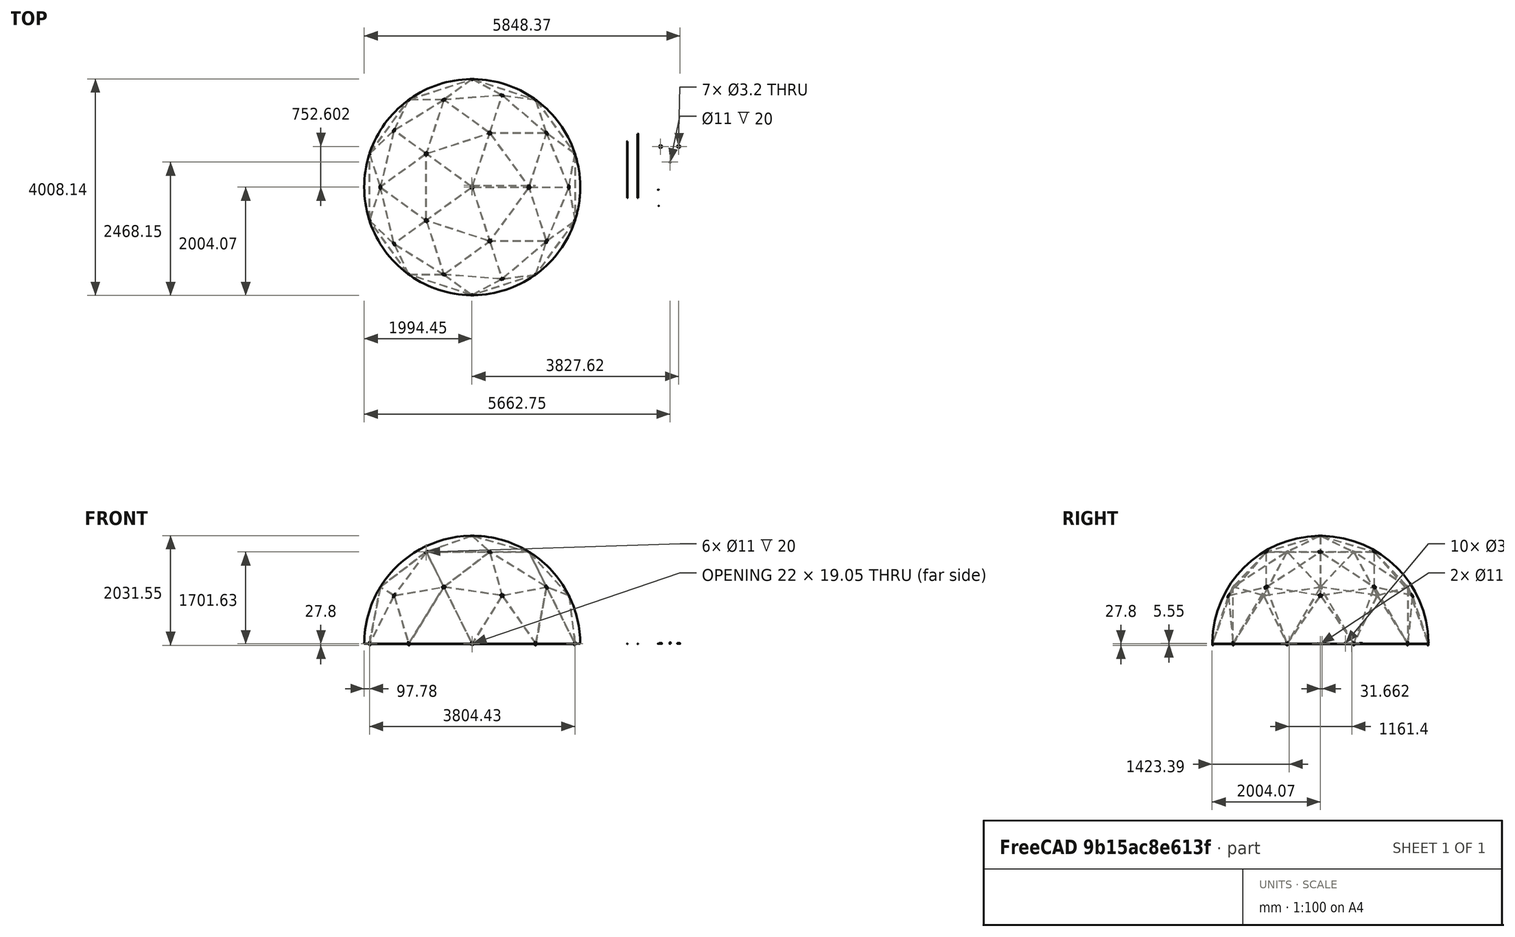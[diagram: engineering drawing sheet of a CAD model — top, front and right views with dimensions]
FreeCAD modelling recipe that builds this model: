
FCSTD DOCUMENT  (FreeCAD 0.19R)
Label: Ejemplo1top
License: All rights reserved
LicenseURL: http://en.wikipedia.org/wiki/All_rights_reserved
objects: Part::Feature×235, Part::Part2DObjectPython×138, App::DocumentObjectGroup×21, App::Annotation×18, Part::Mirroring×7, App::FeaturePython×4, Part::Sphere×1, Part::Cylinder×1
note: 382 computed .brp shape members not serialized (recipe doc carries the construction recipe); baked Part::Feature solids carry a one-line shape summary decoded from their .brp

FEATURE [Part::Part2DObjectPython] Line  # Draft 2D object (typed FeaturePython)
  ChamferSize = 0
  Closed = false
  End = (-1902.16,617.998,0)
  FilletRadius = 0
  Length = 1236.1
  MakeFace = true
  MapMode = 5
  Placement = pos=(-1154.86,1595.54,0) rot=(0,0,-1;0.628319rad)
  Points = (2) [(-30,6,0),(-30,-1230.1,0)]
  Start = (-1175.6,1618.02,0)
  Subdivisions = 0
FEATURE [Part::Part2DObjectPython] Line003  # Draft 2D object (typed FeaturePython)
  ChamferSize = 0
  Closed = false
  End = (-1175.6,1618.02,0)
  FilletRadius = 0
  Length = 1236.1
  MakeFace = true
  MapMode = 5
  Placement = pos=(3.56417,1969.61,0) rot=(0,0,-1;1.25664rad)
  Points = (2) [(-30,6,0),(-30,-1230.1,0)]
  Start = (3.56741e-11,2000,0)
  Subdivisions = 0
FEATURE [Part::Mirroring] Part__Mirroring  label="Line (Mirror #1)"
  Base = (0,0,0)
  Normal = (1,0,0)
  Source = -> Line
FEATURE [Part::Mirroring] Part__Mirroring001  label="Line003 (Mirror #2)"
  Base = (0,0,0)
  Normal = (1,0,0)
  Source = -> Line003
FEATURE [Part::Mirroring] Part__Mirroring002  label="Line (Mirror #3)"
  Base = (0,0,0)
  Normal = (0,1,0)
  Source = -> Line
FEATURE [Part::Mirroring] Part__Mirroring003  label="Line003 (Mirror #4)"
  Base = (0,0,0)
  Normal = (0,1,0)
  Source = -> Line003
FEATURE [Part::Mirroring] Part__Mirroring004  label="Line (Mirror #5)"
  Base = (0,0,0)
  Normal = (0,1,0)
  Source = -> Part__Mirroring
FEATURE [Part::Mirroring] Part__Mirroring005  label="Line003 (Mirror #6)"
  Base = (0,0,0)
  Normal = (0,1,0)
  Source = -> Part__Mirroring001
FEATURE [Part::Part2DObjectPython] Line006  # Draft 2D object (typed FeaturePython)
  ChamferSize = 0
  Closed = false
  End = (-1902.16,-617.998,0)
  FilletRadius = 0
  Length = 1236
  MakeFace = true
  MapMode = 5
  Points = (2) [(-1902.16,617.998,0),(-1902.16,-617.998,0)]
  Start = (-1902.16,617.998,0)
  Subdivisions = 0
FEATURE [Part::Sphere] Sphere
  Angle1 = 0
  Angle2 = 90
  Angle3 = 360
  AttacherType = Attacher::AttachEngine3D
  Radius = 2000
FEATURE [Part::Part2DObjectPython] Line014  # Draft 2D object (typed FeaturePython)
  ChamferSize = 0
  Closed = false
  End = (1902.16,3e-10,0)
  FilletRadius = 0
  Length = 1902.16
  MakeFace = true
  MapMode = 5
  Points = (2) [(-1.99975e-10,3.00133e-10,0),(1902.16,3.0025e-10,0)]
  Start = (0,0,0)
  Subdivisions = 0
FEATURE [Part::Part2DObjectPython] Line015  # Draft 2D object (typed FeaturePython)
  ChamferSize = 0
  Closed = false
  End = (1902.16,3e-10,0)
  FilletRadius = 0
  Length = 1902.16
  MakeFace = true
  MapMode = 5
  Points = (2) [(-1.99975e-10,3.00133e-10,0),(1902.16,3.0025e-10,0)]
  Start = (0,0,0)
  Subdivisions = 0
FEATURE [Part::Part2DObjectPython] Line016  # Draft 2D object (typed FeaturePython)
  ChamferSize = 0
  Closed = false
  End = (587.785,1809.02,0)
  FilletRadius = 0
  Length = 1902.11
  MakeFace = true
  MapMode = 5
  Points = (2) [(-1.99975e-10,3.00133e-10,0),(587.785,1809.02,0)]
  Start = (0,0,0)
  Subdivisions = 0
FEATURE [Part::Part2DObjectPython] Line017  # Draft 2D object (typed FeaturePython)
  ChamferSize = 0
  Closed = false
  End = (-1538.86,1118.05,0)
  FilletRadius = 0
  Length = 1902.13
  MakeFace = true
  MapMode = 5
  Points = (2) [(-1.99975e-10,3.00133e-10,0),(-1538.86,1118.05,0)]
  Start = (0,0,0)
  Subdivisions = 0
FEATURE [Part::Part2DObjectPython] Line018  # Draft 2D object (typed FeaturePython)
  ChamferSize = 0
  Closed = false
  End = (-1538.86,-1118.05,0)
  FilletRadius = 0
  Length = 1902.13
  MakeFace = true
  MapMode = 5
  Points = (2) [(-1.99975e-10,3.00133e-10,0),(-1538.86,-1118.05,0)]
  Start = (0,0,0)
  Subdivisions = 0
FEATURE [Part::Part2DObjectPython] Line019  # Draft 2D object (typed FeaturePython)
  ChamferSize = 0
  Closed = false
  End = (-577.454,-703.099,0)
  FilletRadius = 0
  Length = 1093.1
  MakeFace = true
  MapMode = 5
  Placement = pos=(1075.61,-2380.95,0) rot=(0,0,-1;0.581932rad)
  Points = (2) [(-2300,-600,0),(-2303.19,493.095,0)]
  Start = (-1175.6,-1618.02,0)
  Subdivisions = 0
FEATURE [Part::Part2DObjectPython] Line022  # Draft 2D object (typed FeaturePython)
  ChamferSize = 0
  Closed = false
  End = (587.8,-1809.01,0)
  FilletRadius = 0
  Length = 1902.11
  MakeFace = true
  MapMode = 5
  Points = (2) [(-1.99975e-10,3.00133e-10,0),(587.8,-1809.01,0)]
  Start = (0,0,0)
  Subdivisions = 0
FEATURE [Part::Part2DObjectPython] Line023  # Draft 2D object (typed FeaturePython)
  ChamferSize = 0
  Closed = false
  End = (0,0,2000)
  FilletRadius = 0
  Length = 2000
  MakeFace = true
  MapMode = 5
  Points = (2) [(-1.99975e-10,3.00133e-10,0),(1.22465e-13,-2.99952e-29,2000)]
  Start = (0,0,0)
  Subdivisions = 0
FEATURE [Part::Part2DObjectPython] DWire001  # Draft 2D object (typed FeaturePython)
  ChamferSize = 0
  Closed = true
  End = (1902.16,617.998,0)
  FilletRadius = 0
  Length = 3422.2
  MakeFace = true
  MapMode = 5
  Points = (3) [(1902.16,-617.998,0),(1788.83,-9.64734e-10,894.484),(1902.16,617.998,0)]
  Start = (1902.16,-617.998,0)
  Subdivisions = 0
FEATURE [Part::Part2DObjectPython] DWire  # Draft 2D object (typed FeaturePython)
  ChamferSize = 0
  Closed = true
  End = (587.785,1809.02,0)
  FilletRadius = 0
  Length = 6662.19
  MakeFace = true
  MapMode = 5
  Points = (3) [(1.22465e-13,0,2000),(-1.99975e-10,3.00133e-10,0),(587.785,1809.02,0)]
  Start = (0,0,2000)
  Subdivisions = 0
FEATURE [Part::Mirroring] Part__Mirroring006  label="DWire003 (Mirror #7)"
  Base = (0,0,0)
  Normal = (0,1,0)
FEATURE [Part::Part2DObjectPython] Arc  # Draft 2D object (typed FeaturePython)
  FirstAngle = 56.8247
  LastAngle = 105.817
  MakeFace = true
  MapMode = 5
  Placement = pos=(-1175.6,-1618.02,0) rot=(0,0,1;0rad)
  Radius = 1093.1
FEATURE [Part::Part2DObjectPython] Line026  # Draft 2D object (typed FeaturePython)
  ChamferSize = 0
  Closed = false
  End = (-1902.16,-617.998,0)
  FilletRadius = 0
  Length = 1093.15
  MakeFace = true
  MapMode = 5
  Points = (2) [(-809.424,-588.081,0),(-1902.16,-617.998,0)]
  Start = (-809.424,-588.081,0)
  Subdivisions = 0
FEATURE [Part::Part2DObjectPython] DWire004  # Draft 2D object (typed FeaturePython)
  ChamferSize = 0
  Closed = true
  End = (-1538.86,-1118.05,0)
  FilletRadius = 0
  Length = 6662.22
  MakeFace = true
  MapMode = 5
  Points = (3) [(1.22465e-13,0,2000),(-1.99975e-10,3.00133e-10,0),(-1538.86,-1118.05,0)]
  Start = (0,0,2000)
  Subdivisions = 0
FEATURE [Part::Part2DObjectPython] DWire005  # Draft 2D object (typed FeaturePython)
  ChamferSize = 0
  Closed = true
  End = (-1175.6,-1618.02,0)
  FilletRadius = 0
  Length = 3422.35
  MakeFace = true
  MapMode = 5
  Points = (3) [(-1902.16,-617.998,0),(-1447.19,-1051.45,894.481),(-1175.6,-1618.02,0)]
  Start = (-1902.16,-617.998,0)
  Subdivisions = 0
FEATURE [Part::Part2DObjectPython] Line027  # Draft 2D object (typed FeaturePython)
  ChamferSize = 0
  Closed = false
  End = (-878.683,234.127,0)
  FilletRadius = 0
  Length = 1093.1
  MakeFace = true
  MapMode = 5
  Placement = pos=(-2154.97,-1745.49,0) rot=(0,0,-1;1.93254rad)
  Points = (2) [(-2300,-600,0),(-2303.19,493.095,0)]
  Start = (-1902.16,617.998,0)
  Subdivisions = 0
FEATURE [Part::Part2DObjectPython] Arc003  # Draft 2D object (typed FeaturePython)
  FirstAngle = -20.5593
  LastAngle = 28.7005
  MakeFace = true
  MapMode = 5
  Placement = pos=(-1902.16,617.998,0) rot=(0,0,1;0rad)
  Radius = 1093.1
FEATURE [Part::Part2DObjectPython] DWire006  # Draft 2D object (typed FeaturePython)
  ChamferSize = 0
  Closed = true
  End = (-1538.86,1118.05,0)
  FilletRadius = 0
  Length = 6662.22
  MakeFace = true
  MapMode = 5
  Points = (3) [(1.22465e-13,0,2000),(-1.99975e-10,3.00133e-10,0),(-1538.86,1118.05,0)]
  Start = (0,0,2000)
  Subdivisions = 0
FEATURE [Part::Part2DObjectPython] DWire007  # Draft 2D object (typed FeaturePython)
  ChamferSize = 0
  Closed = true
  End = (-1902.16,617.998,0)
  FilletRadius = 0
  Length = 3422.25
  MakeFace = true
  MapMode = 5
  Points = (3) [(-1175.6,1618.02,0),(-1447.21,1051.46,894.426),(-1902.16,617.998,0)]
  Start = (-1175.6,1618.02,0)
  Subdivisions = 0
FEATURE [Part::Part2DObjectPython] DWire008  # Draft 2D object (typed FeaturePython)
  ChamferSize = 0
  Closed = true
  End = (324.937,-1000.03,1701.28)
  FilletRadius = 0
  Length = 3422.31
  MakeFace = true
  MapMode = 5
  Points = (3) [(2.23523e-10,2.82703e-10,2000),(-850.675,-618.052,1701.28),(324.937,-1000.03,1701.28)]
  Start = (2.24e-10,2.83e-10,2000)
  Subdivisions = 0
FEATURE [Part::Part2DObjectPython] DWire009  # Draft 2D object (typed FeaturePython)
  ChamferSize = 0
  Closed = true
  End = (-2e-10,3e-10,2000)
  FilletRadius = 0
  Length = 3422.3
  MakeFace = true
  MapMode = 5
  Points = (3) [(324.937,-1000.03,1701.28),(1051.49,1.3321e-09,1701.28),(-1.99876e-10,3.00061e-10,2000)]
  Start = (324.937,-1000.03,1701.28)
  Subdivisions = 0
FEATURE [Part::Part2DObjectPython] DWire010  # Draft 2D object (typed FeaturePython)
  ChamferSize = 0
  Closed = true
  End = (324.929,1000.03,1701.28)
  FilletRadius = 0
  Length = 3422.3
  MakeFace = true
  MapMode = 5
  Points = (3) [(-1.99876e-10,3.00061e-10,2000),(1051.49,1.3321e-09,1701.28),(324.929,1000.03,1701.28)]
  Start = (-2e-10,3e-10,2000)
  Subdivisions = 0
FEATURE [Part::Part2DObjectPython] DWire011  # Draft 2D object (typed FeaturePython)
  ChamferSize = 0
  Closed = true
  End = (-850.675,618.052,1701.28)
  FilletRadius = 0
  Length = 3422.3
  MakeFace = true
  MapMode = 5
  Points = (3) [(-1.99876e-10,3.00061e-10,2000),(324.929,1000.03,1701.28),(-850.675,618.052,1701.28)]
  Start = (-2e-10,3e-10,2000)
  Subdivisions = 0
FEATURE [Part::Part2DObjectPython] DWire012  # Draft 2D object (typed FeaturePython)
  ChamferSize = 0
  Closed = true
  End = (-850.675,-618.052,1701.28)
  FilletRadius = 0
  Length = 3422.3
  MakeFace = true
  MapMode = 5
  Points = (3) [(-1.99876e-10,3.00061e-10,2000),(-850.675,618.052,1701.28),(-850.675,-618.052,1701.28)]
  Start = (-2e-10,3e-10,2000)
  Subdivisions = 0
FEATURE [Part::Part2DObjectPython] Line040  # Draft 2D object (typed FeaturePython)
  ChamferSize = 0
  Closed = false
  End = (-1447.19,-1051.45,894.481)
  FilletRadius = 0
  Length = 1092.97
  MakeFace = true
  MapMode = 5
  Points = (2) [(-850.675,-618.052,1701.28),(-1447.19,-1051.45,894.481)]
  Start = (-850.675,-618.052,1701.28)
  Subdivisions = 0
FEATURE [Part::Part2DObjectPython] DWire013  # Draft 2D object (typed FeaturePython)
  ChamferSize = 0
  Closed = true
  End = (0,0,2000)
  FilletRadius = 0
  Length = 6662.22
  MakeFace = true
  MapMode = 5
  Points = (3) [(1538.88,-1118.01,0),(-1.99975e-10,3.00133e-10,0),(1.22465e-13,0,2000)]
  Start = (1538.88,-1118.01,0)
  Subdivisions = 0
FEATURE [Part::Part2DObjectPython] Arc007  # Draft 2D object (typed FeaturePython)
  FirstAngle = -90
  LastAngle = 6.05971
  MakeFace = true
  MapMode = 5
  Placement = pos=(7.36405e-11,1.01362e-10,0) rot=(0.223911,0.689153,0.689153;2.70104rad)
  Radius = 2000
  Support = -> [DWire013]
FEATURE [Part::Part2DObjectPython] DWire014  # Draft 2D object (typed FeaturePython)
  ChamferSize = 0
  Closed = true
  End = (1902.16,-617.998,0)
  FilletRadius = 0
  Length = 3708.32
  MakeFace = true
  MapMode = 5
  Points = (3) [(1175.6,-1618.02,0),(1376.39,-999.957,1051.5),(1902.16,-617.998,0)]
  Start = (1175.6,-1618.02,0)
  Subdivisions = 0
FEATURE [Part::Part2DObjectPython] DWire015  # Draft 2D object (typed FeaturePython)
  ChamferSize = 0
  Closed = true
  End = (1051.49,1.332e-09,1701.28)
  FilletRadius = 0
  Length = 3708.12
  MakeFace = true
  MapMode = 5
  Points = (3) [(1376.39,-999.957,1051.5),(324.937,-1000.03,1701.28),(1051.49,1.3321e-09,1701.28)]
  Start = (1376.39,-999.957,1051.5)
  Subdivisions = 0
FEATURE [Part::Part2DObjectPython] DWire016  # Draft 2D object (typed FeaturePython)
  ChamferSize = 0
  Closed = true
  End = (1175.6,-1618.02,0)
  FilletRadius = 0
  Length = 3422.29
  MakeFace = true
  MapMode = 5
  Points = (3) [(552.796,-1701.28,894.456),(1376.39,-999.957,1051.5),(1175.6,-1618.02,0)]
  Start = (552.796,-1701.28,894.456)
  Subdivisions = 0
FEATURE [Part::Part2DObjectPython] DWire017  # Draft 2D object (typed FeaturePython)
  ChamferSize = 0
  Closed = true
  End = (1902.16,-617.998,0)
  FilletRadius = 0
  Length = 3422.23
  MakeFace = true
  MapMode = 5
  Points = (3) [(1376.39,-999.957,1051.5),(1788.83,-9.64734e-10,894.484),(1902.16,-617.998,0)]
  Start = (1376.39,-999.957,1051.5)
  Subdivisions = 0
FEATURE [Part::Part2DObjectPython] DWire018  # Draft 2D object (typed FeaturePython)
  ChamferSize = 0
  Closed = true
  End = (1376.39,-999.957,1051.5)
  FilletRadius = 0
  Length = 3422.11
  MakeFace = true
  MapMode = 5
  Points = (3) [(324.937,-1000.03,1701.28),(552.796,-1701.28,894.456),(1376.39,-999.957,1051.5)]
  Start = (324.937,-1000.03,1701.28)
  Subdivisions = 0
FEATURE [Part::Part2DObjectPython] DWire019  # Draft 2D object (typed FeaturePython)
  ChamferSize = 0
  Closed = true
  End = (1788.83,-9.65e-10,894.484)
  FilletRadius = 0
  Length = 3421.98
  MakeFace = true
  MapMode = 5
  Points = (3) [(1376.39,-999.957,1051.5),(1051.49,1.3321e-09,1701.28),(1788.83,-9.64734e-10,894.484)]
  Start = (1376.39,-999.957,1051.5)
  Subdivisions = 0
FEATURE [Part::Part2DObjectPython] DWire020  # Draft 2D object (typed FeaturePython)
  ChamferSize = 0
  Closed = true
  End = (1175.6,1618.02,0)
  FilletRadius = 0
  Length = 3708.32
  MakeFace = true
  MapMode = 5
  Points = (3) [(1902.16,617.998,0),(1376.39,999.957,1051.5),(1175.6,1618.02,0)]
  Start = (1902.16,617.998,0)
  Subdivisions = 0
FEATURE [Part::Part2DObjectPython] DWire021  # Draft 2D object (typed FeaturePython)
  ChamferSize = 0
  Closed = true
  End = (-1175.6,1618.02,0)
  FilletRadius = 0
  Length = 3708.32
  MakeFace = true
  MapMode = 5
  Points = (3) [(-525.738,1618.01,1051.5),(3.56977e-11,2000,0),(-1175.6,1618.02,0)]
  Start = (-525.738,1618.01,1051.5)
  Subdivisions = 0
FEATURE [Part::Part2DObjectPython] DWire022  # Draft 2D object (typed FeaturePython)
  ChamferSize = 0
  Closed = true
  End = (-1902.16,-617.998,0)
  FilletRadius = 0
  Length = 3708.18
  MakeFace = true
  MapMode = 5
  Points = (3) [(-1701.28,-1.02242e-09,1051.5),(-1902.16,617.998,0),(-1902.16,-617.998,0)]
  Start = (-1701.28,-1.022e-09,1051.5)
  Subdivisions = 0
FEATURE [Part::Part2DObjectPython] DWire023  # Draft 2D object (typed FeaturePython)
  ChamferSize = 0
  Closed = true
  End = (-3.6e-11,-2000,0)
  FilletRadius = 0
  Length = 3708.32
  MakeFace = true
  MapMode = 5
  Points = (3) [(-525.738,-1618.01,1051.5),(-1175.6,-1618.02,0),(-3.5925e-11,-2000,0)]
  Start = (-525.738,-1618.01,1051.5)
  Subdivisions = 0
FEATURE [Part::Part2DObjectPython] DWire024  # Draft 2D object (typed FeaturePython)
  ChamferSize = 0
  Closed = true
  End = (324.929,1000.03,1701.28)
  FilletRadius = 0
  Length = 3708.14
  MakeFace = true
  MapMode = 5
  Points = (3) [(1051.49,1.3321e-09,1701.28),(1376.39,999.957,1051.5),(324.929,1000.03,1701.28)]
  Start = (1051.49,1.332e-09,1701.28)
  Subdivisions = 0
FEATURE [Part::Part2DObjectPython] DWire025  # Draft 2D object (typed FeaturePython)
  ChamferSize = 0
  Closed = true
  End = (1376.39,999.957,1051.5)
  FilletRadius = 0
  Length = 3421.98
  MakeFace = true
  MapMode = 5
  Points = (3) [(1051.49,1.3321e-09,1701.28),(1788.83,-9.64734e-10,894.484),(1376.39,999.957,1051.5)]
  Start = (1051.49,1.332e-09,1701.28)
  Subdivisions = 0
FEATURE [Part::Part2DObjectPython] DWire026  # Draft 2D object (typed FeaturePython)
  ChamferSize = 0
  Closed = true
  End = (1376.39,999.957,1051.5)
  FilletRadius = 0
  Length = 3422.23
  MakeFace = true
  MapMode = 5
  Points = (3) [(1788.83,-9.64734e-10,894.484),(1902.16,617.998,0),(1376.39,999.957,1051.5)]
  Start = (1788.83,-9.65e-10,894.484)
  Subdivisions = 0
FEATURE [Part::Part2DObjectPython] DWire027  # Draft 2D object (typed FeaturePython)
  ChamferSize = 0
  Closed = true
  End = (552.796,1701.28,894.456)
  FilletRadius = 0
  Length = 3422.29
  MakeFace = true
  MapMode = 5
  Points = (3) [(1376.39,999.957,1051.5),(1175.6,1618.02,0),(552.796,1701.28,894.456)]
  Start = (1376.39,999.957,1051.5)
  Subdivisions = 0
FEATURE [Part::Part2DObjectPython] DWire028  # Draft 2D object (typed FeaturePython)
  ChamferSize = 0
  Closed = true
  End = (552.796,1701.28,894.456)
  FilletRadius = 0
  Length = 3422.12
  MakeFace = true
  MapMode = 5
  Points = (3) [(324.929,1000.03,1701.28),(1376.39,999.957,1051.5),(552.796,1701.28,894.456)]
  Start = (324.929,1000.03,1701.28)
  Subdivisions = 0
FEATURE [Part::Part2DObjectPython] DWire029  # Draft 2D object (typed FeaturePython)
  ChamferSize = 0
  Closed = true
  End = (-3.6e-11,2000,0)
  FilletRadius = 0
  Length = 3422.29
  MakeFace = true
  MapMode = 5
  Points = (3) [(-525.738,1618.01,1051.5),(552.796,1701.28,894.456),(-3.5925e-11,2000,0)]
  Start = (-525.738,1618.01,1051.5)
  Subdivisions = 0
FEATURE [Part::Part2DObjectPython] DWire030  # Draft 2D object (typed FeaturePython)
  ChamferSize = 0
  Closed = true
  End = (-525.738,1618.01,1051.5)
  FilletRadius = 0
  Length = 3422.11
  MakeFace = true
  MapMode = 5
  Points = (3) [(324.929,1000.03,1701.28),(552.796,1701.28,894.456),(-525.738,1618.01,1051.5)]
  Start = (324.929,1000.03,1701.28)
  Subdivisions = 0
FEATURE [Part::Part2DObjectPython] DWire031  # Draft 2D object (typed FeaturePython)
  ChamferSize = 0
  Closed = true
  End = (-850.675,618.052,1701.28)
  FilletRadius = 0
  Length = 3708.14
  MakeFace = true
  MapMode = 5
  Points = (3) [(324.929,1000.03,1701.28),(-525.738,1618.01,1051.5),(-850.675,618.052,1701.28)]
  Start = (324.929,1000.03,1701.28)
  Subdivisions = 0
FEATURE [Part::Part2DObjectPython] DWire032  # Draft 2D object (typed FeaturePython)
  ChamferSize = 0
  Closed = true
  End = (-1447.21,1051.46,894.426)
  FilletRadius = 0
  Length = 3422.21
  MakeFace = true
  MapMode = 5
  Points = (3) [(-525.738,1618.01,1051.5),(-1175.6,1618.02,0),(-1447.21,1051.46,894.426)]
  Start = (-525.738,1618.01,1051.5)
  Subdivisions = 0
FEATURE [Part::Part2DObjectPython] DWire033  # Draft 2D object (typed FeaturePython)
  ChamferSize = 0
  Closed = true
  End = (-1447.21,1051.46,894.426)
  FilletRadius = 0
  Length = 3422.1
  MakeFace = true
  MapMode = 5
  Points = (3) [(-525.738,1618.01,1051.5),(-850.675,618.052,1701.28),(-1447.21,1051.46,894.426)]
  Start = (-525.738,1618.01,1051.5)
  Subdivisions = 0
FEATURE [Part::Part2DObjectPython] DWire034  # Draft 2D object (typed FeaturePython)
  ChamferSize = 0
  Closed = true
  End = (-1701.28,-1.022e-09,1051.5)
  FilletRadius = 0
  Length = 3422.12
  MakeFace = true
  MapMode = 5
  Points = (3) [(-850.675,618.052,1701.28),(-1447.21,1051.46,894.426),(-1701.28,-1.02242e-09,1051.5)]
  Start = (-850.675,618.052,1701.28)
  Subdivisions = 0
FEATURE [Part::Part2DObjectPython] DWire035  # Draft 2D object (typed FeaturePython)
  ChamferSize = 0
  Closed = true
  End = (-1701.28,-1.022e-09,1051.5)
  FilletRadius = 0
  Length = 3422.26
  MakeFace = true
  MapMode = 5
  Points = (3) [(-1447.21,1051.46,894.426),(-1902.16,617.998,0),(-1701.28,-1.02242e-09,1051.5)]
  Start = (-1447.21,1051.46,894.426)
  Subdivisions = 0
FEATURE [Part::Part2DObjectPython] DWire036  # Draft 2D object (typed FeaturePython)
  ChamferSize = 0
  Closed = true
  End = (-850.675,-618.052,1701.28)
  FilletRadius = 0
  Length = 3708.14
  MakeFace = true
  MapMode = 5
  Points = (3) [(-850.675,618.052,1701.28),(-1701.28,-1.02242e-09,1051.5),(-850.675,-618.052,1701.28)]
  Start = (-850.675,618.052,1701.28)
  Subdivisions = 0
FEATURE [Part::Part2DObjectPython] DWire037  # Draft 2D object (typed FeaturePython)
  ChamferSize = 0
  Closed = true
  End = (-1447.19,-1051.45,894.481)
  FilletRadius = 0
  Length = 3422.04
  MakeFace = true
  MapMode = 5
  Points = (3) [(-1701.28,-1.02242e-09,1051.5),(-850.675,-618.052,1701.28),(-1447.19,-1051.45,894.481)]
  Start = (-1701.28,-1.022e-09,1051.5)
  Subdivisions = 0
FEATURE [Part::Part2DObjectPython] DWire038  # Draft 2D object (typed FeaturePython)
  ChamferSize = 0
  Closed = true
  End = (-1447.19,-1051.45,894.481)
  FilletRadius = 0
  Length = 3422.29
  MakeFace = true
  MapMode = 5
  Points = (3) [(-1701.28,-1.02242e-09,1051.5),(-1902.16,-617.998,0),(-1447.19,-1051.45,894.481)]
  Start = (-1701.28,-1.022e-09,1051.5)
  Subdivisions = 0
FEATURE [Part::Part2DObjectPython] DWire039  # Draft 2D object (typed FeaturePython)
  ChamferSize = 0
  Closed = true
  End = (-525.738,-1618.01,1051.5)
  FilletRadius = 0
  Length = 3422.02
  MakeFace = true
  MapMode = 5
  Points = (3) [(-850.675,-618.052,1701.28),(-1447.19,-1051.45,894.481),(-525.738,-1618.01,1051.5)]
  Start = (-850.675,-618.052,1701.28)
  Subdivisions = 0
FEATURE [Part::Part2DObjectPython] DWire040  # Draft 2D object (typed FeaturePython)
  ChamferSize = 0
  Closed = true
  End = (324.937,-1000.03,1701.28)
  FilletRadius = 0
  Length = 3708.15
  MakeFace = true
  MapMode = 5
  Points = (3) [(-850.675,-618.052,1701.28),(-525.738,-1618.01,1051.5),(324.937,-1000.03,1701.28)]
  Start = (-850.675,-618.052,1701.28)
  Subdivisions = 0
FEATURE [Part::Part2DObjectPython] DWire041  # Draft 2D object (typed FeaturePython)
  ChamferSize = 0
  Closed = true
  End = (-1447.19,-1051.45,894.481)
  FilletRadius = 0
  Length = 3422.24
  MakeFace = true
  MapMode = 5
  Points = (3) [(-525.738,-1618.01,1051.5),(-1175.6,-1618.02,0),(-1447.19,-1051.45,894.481)]
  Start = (-525.738,-1618.01,1051.5)
  Subdivisions = 0
FEATURE [Part::Part2DObjectPython] DWire042  # Draft 2D object (typed FeaturePython)
  ChamferSize = 0
  Closed = true
  End = (552.796,-1701.28,894.456)
  FilletRadius = 0
  Length = 3422.12
  MakeFace = true
  MapMode = 5
  Points = (3) [(-525.738,-1618.01,1051.5),(324.937,-1000.03,1701.28),(552.796,-1701.28,894.456)]
  Start = (-525.738,-1618.01,1051.5)
  Subdivisions = 0
FEATURE [Part::Part2DObjectPython] DWire043  # Draft 2D object (typed FeaturePython)
  ChamferSize = 0
  Closed = true
  End = (552.796,-1701.28,894.456)
  FilletRadius = 0
  Length = 3422.29
  MakeFace = true
  MapMode = 5
  Points = (3) [(-525.738,-1618.01,1051.5),(-3.5925e-11,-2000,0),(552.796,-1701.28,894.456)]
  Start = (-525.738,-1618.01,1051.5)
  Subdivisions = 0
FEATURE [App::DocumentObjectGroup] Group001  label="Top-pentagon"
  Group = -> [DWire010,DWire011,DWire012,DWire008,DWire009]
FEATURE [App::DocumentObjectGroup] Group002  label="Pentagon-1"
  Group = -> [DWire019,DWire025,DWire026,DWire001,DWire017]
FEATURE [App::DocumentObjectGroup] Group003  label="Pentagon-2"
  Group = -> [DWire028,DWire030,DWire029,Part__Mirroring006,DWire027]
FEATURE [App::DocumentObjectGroup] Group004  label="Pentagon-3"
  Group = -> [DWire033,DWire034,DWire035,DWire007,DWire032]
FEATURE [App::DocumentObjectGroup] Group005  label="Pentagon-4"
  Group = -> [DWire037,DWire038,DWire005,DWire041,Line040,DWire039]
FEATURE [Part::Part2DObjectPython] DWire044  # Draft 2D object (typed FeaturePython)
  ChamferSize = 0
  Closed = true
  End = (1175.6,-1618.02,0)
  FilletRadius = 0
  Length = 3422.3
  MakeFace = true
  MapMode = 5
  Points = (3) [(-3.5925e-11,-2000,0),(552.796,-1701.28,894.456),(1175.6,-1618.02,0)]
  Start = (-3.6e-11,-2000,0)
  Subdivisions = 0
FEATURE [App::DocumentObjectGroup] Group006  label="Pentagon-5"
  Group = -> [DWire042,DWire043,DWire016,DWire018,DWire044]
FEATURE [App::DocumentObjectGroup] Group007  label="Aux"
  Group = -> [Part__Mirroring002,Part__Mirroring003,Part__Mirroring004,Part__Mirroring005,Line006,Line014,Line015,Line016,Line017,Line018,Line019,Line022,Line023,DWire,Arc,Line026,DWire004,Line027,Arc003,DWire006,DWire013,Arc007,Sphere]
FEATURE [Part::Part2DObjectPython] DWire045  label="Bottom"  # Draft 2D object (typed FeaturePython)
  ChamferSize = 0
  Closed = true
  End = (1902.16,-617.998,0)
  FilletRadius = 0
  Length = 12360.8
  MakeFace = true
  MapMode = 5
  Points = (10) [(1902.16,617.998,0),(1175.6,1618.02,0),(3.56977e-11,2000,0),(-1175.6,1618.02,0),(-1902.16,617.998,0),(-1902.16,-617.998,0),(-1175.6,-1618.02,0),+3 more]
  Start = (1902.16,617.998,0)
  Subdivisions = 0
FEATURE [App::DocumentObjectGroup] Group008  label="Green-triangles"
  Group = -> [DWire023,DWire040,DWire015,DWire014,DWire024,DWire031,DWire036,DWire022,DWire021,DWire020]
FEATURE [Part::Feature] Clone002  label="Hub-007"
  Placement = pos=(1044.95,2.82704e-10,1690.69) rot=(0.191324,0.71403,0.673466;0.757331rad)
  shape: bbox 49.68 x 55.6 x 37.22 mm, 28 faces (baked)
FEATURE [Part::Feature] Clone005  label="strutcap004"
  Placement = pos=(1066.92,2.82878e-10,1684.4) rot=(0.932253,0,0.361806;3.14159rad)
  shape: bbox 31.1 x 20 x 29.82 mm, 19 faces (baked)
FEATURE [Part::Feature] Clone008  label="strutcap007"
  Placement = pos=(1038.85,-19.0526,1701.75) rot=(0.667656,-0.64473,0.372235;1.42598rad)
  shape: bbox 25.29 x 31.07 x 25.73 mm, 19 faces (baked)
FEATURE [Part::Feature] Clone009  label="strutcap008"
  Placement = pos=(1029.49,2.82532e-10,1707.53) rot=(0,-1,0;1.294rad)
  shape: bbox 31.29 x 20 x 25.37 mm, 19 faces (baked)
FEATURE [Part::Feature] Clone028  label="strutcap025"
  Placement = pos=(1902.2,-594.877,0) rot=(-1,-1.4e-05,1.4e-05;1.5708rad)
  shape: bbox 20.3 x 30 x 20 mm, 19 faces (baked)
FEATURE [Part::Feature] Clone030  label="strutcap027"
  Placement = pos=(1888.76,-636.496,-2.5e-14) rot=(0.909046,-0.294649,-0.294649;1.66601rad)
  shape: bbox 27.81 x 32.24 x 20 mm, 19 faces (baked)
FEATURE [Part::Feature] Clone031  label="Hub-012"
  Placement = pos=(1889.5,-613.884,-5e-15) rot=(0.154555,0.97582,-0.154555;1.59527rad)
  shape: bbox 27.47 x 52.09 x 55.6 mm, 28 faces (baked)
FEATURE [Part::Feature] Cylinder014  label="Varilla-B-modif-003"
  Placement = pos=(1902.16,593.953,-2.89e-13) rot=(1,1.4e-05,1.4e-05;1.5708rad)
  shape: bbox 10.03 x 1189 x 10 mm, 3 faces (baked)
FEATURE [App::DocumentObjectGroup] Group012
FEATURE [App::DocumentObjectGroup] Group  label="Domo-superficies"
  Group = -> [Group001,Group002,Group003,Group004,Group005,Group006,Group008,DWire045,Group012]
FEATURE [Part::Feature] Clone001004  label="Hub5-01-clave002"
  Placement = pos=(-1.81309e-05,2.82703e-10,1987.55) rot=(0,0,-1;0.314151rad)
  shape: bbox 54.38 x 55.6 x 12.4 mm, 25 faces (baked)
FEATURE [Part::Feature] Clone  label="strutcap031"
  Placement = pos=(22.0001,2.82694e-10,1993.75) rot=(0.797896,0,0.602796;3.14159rad)
  shape: bbox 32.05 x 20 x 22.68 mm, 19 faces (baked)
FEATURE [Part::Feature] Clone001005  label="Hub5-01-clave003"
  Placement = pos=(1777.69,2.82703e-10,888.915) rot=(0.523905,0.082976,0.847726;2.87466rad)
  shape: bbox 33.84 x 55.6 x 51.33 mm, 25 faces (baked)
FEATURE [Part::Feature] Clone001006  label="strutcap032"
  Placement = pos=(1773.4,2.82716e-10,911.365) rot=(0,-1,0;0.740475rad)
  shape: bbox 29.03 x 20 x 31.71 mm, 19 faces (baked)
FEATURE [Part::Feature] Clone001007  label="Hub-014"
  Placement = pos=(1889.5,613.885,-5e-15) rot=(-0.154531,0.975828,0.154531;1.59526rad)
  shape: bbox 27.47 x 52.09 x 55.6 mm, 28 faces (baked)
FEATURE [Part::Feature] Clone001008  label="strutcap033"
  Placement = pos=(1902.19,595.158,-2.5e-14) rot=(1,0.00069,0.00069;1.5708rad)
  shape: bbox 20.33 x 30.01 x 20 mm, 19 faces (baked)
FEATURE [Part::Feature] Clone001009  label="strutcap034"
  Placement = pos=(1888.6,636.724,0) rot=(-0.908667,-0.295233,0.295233;1.66643rad)
  shape: bbox 27.82 x 32.23 x 20 mm, 19 faces (baked)
FEATURE [Part::Feature] Clone001010  label="strutcap035"
  Placement = pos=(1899.8,-604.923,18.9221) rot=(-0.98127,-0.136231,0.136202;0.618302rad)
  shape: bbox 20 x 28.03 x 30.96 mm, 19 faces (baked)
FEATURE [Part::Feature] Clone001012  label="strutcap037"
  Placement = pos=(1791.2,-12.9311,875.769) rot=(0.998074,0.043631,0.044104;2.5353rad)
  shape: bbox 22.47 x 27.49 x 30.68 mm, 19 faces (baked)
FEATURE [Part::Cylinder] Cylinder015  label="Cylinder084"
  Angle = 360
  AttacherType = Attacher::AttachEngine3D
  Height = 1047.11
  Placement = pos=(1066.92,2.82853e-10,1684.4) rot=(0.681894,-0.681894,0.264655;3.65904rad)
  Radius = 5
FEATURE [Part::Feature] Cylinder016  label="Cylinder001"
  Placement = pos=(1791.23,-12.9283,875.771) rot=(0.998113,0.043415,0.043415;2.53525rad)
  shape: bbox 118.5 x 600.2 x 862.6 mm, 3 faces (baked)
FEATURE [Part::Feature] Clone001013  label="strutcap038"
  Placement = pos=(1791.12,13.8918,876.408) rot=(0.993179,0.082001,0.082896;3.73273rad)
  shape: bbox 22.73 x 28.03 x 30.67 mm, 19 faces (baked)
FEATURE [Part::Feature] Cylinder017  label="Cylinder002"
  Placement = pos=(1791.15,13.8946,876.414) rot=(0.993219,0.08221,0.08221;3.73262rad)
  shape: bbox 118.5 x 600.7 x 862.3 mm, 3 faces (baked)
FEATURE [Part::Feature] Clone001014  label="strutcap039"
  Placement = pos=(1899.68,606.357,19.8831) rot=(0.934186,-0.252314,0.25226;0.634069rad)
  shape: bbox 20 x 27.5 x 31.62 mm, 19 faces (baked)
FEATURE [Part::Feature] Cylinder018  label="Cylinder003"
  Placement = pos=(22.0001,2.82669e-10,1993.75) rot=(-0.623692,0.623692,-0.471188;2.26093rad)
  shape: bbox 1010 x 10 x 295.8 mm, 3 faces (baked)
FEATURE [Part::Feature] Cylinder019  label="Cylinder004"
  Placement = pos=(6.79821,20.9234,1993.75) rot=(-0.980863,0.155349,-0.117363;1.86613rad)
  shape: bbox 320.8 x 962 x 295.8 mm, 3 faces (baked)
FEATURE [Part::Feature] Clone001015  label="strutcap040"
  Placement = pos=(6.79821,20.9234,1993.75) rot=(0.690291,0.501531,0.521503;3.86596rad)
  shape: bbox 23.54 x 32.47 x 22.68 mm, 19 faces (baked)
FEATURE [Part::Feature] Clone001016  label="strutcap041"
  Placement = pos=(318.122,979.108,1707.53) rot=(0.463915,-0.638519,0.614065;1.73821rad)
  shape: bbox 23.11 x 31.33 x 25.37 mm, 19 faces (baked)
FEATURE [Part::Feature] Clone001018  label="Hub-015"
  Placement = pos=(322.898,993.806,1690.69) rot=(-0.123041,0.320528,0.939214;1.84115rad)
  shape: bbox 55.11 x 51.63 x 37.22 mm, 28 faces (baked)
FEATURE [Part::Feature] Clone001020  label="strutcap044"
  Placement = pos=(339.134,982.12,1701.75) rot=(0.773329,-0.182879,0.607056;2.21695rad)
  shape: bbox 29.76 x 30.45 x 20.75 mm, 19 faces (baked)
FEATURE [Part::Feature] Clone007  label="strutcap006"
  Placement = pos=(1038.85,19.0526,1701.75) rot=(-0.64113,-0.730539,-0.235086;1.6431rad)
  shape: bbox 27.52 x 31.98 x 20.74 mm, 19 faces (baked)
FEATURE [Part::Feature] Cylinder020  label="Varilla-B-modif-004"
  Placement = pos=(340.068,980.833,1701.75) rot=(0.90866,0.295244,0.295244;1.66644rad)
  shape: bbox 706.9 x 967.7 x 10 mm, 3 faces (baked)
FEATURE [Part::Feature] Clone001023  label="Hub-016"
  Placement = pos=(1367.83,993.738,1044.94) rot=(0.480375,0.156077,0.863064;3.68838rad)
  shape: bbox 46.36 x 51.63 x 50.11 mm, 28 faces (baked)
FEATURE [Part::Feature] Clone001027  label="strutcap049"
  Placement = pos=(1385.02,979.037,1048.2) rot=(0.929901,-0.068235,0.361425;1.8922rad)
  shape: bbox 27.6 x 31.33 x 20.3 mm, 19 faces (baked)
FEATURE [Part::Feature] Clone001030  label="strutcap052"
  Placement = pos=(1779.91,20.6545,898.82) rot=(-0.909103,-0.414228,-0.044114;1.42856rad)
  shape: bbox 24.46 x 32.53 x 22.38 mm, 19 faces (baked)
FEATURE [Part::Feature] Cylinder021  label="Cylinder005"
  Placement = pos=(1779.94,20.6643,898.834) rot=(-0.908834,-0.414887,-0.043473;1.42913rad)
  shape: bbox 403.8 x 962.4 x 159.4 mm, 3 faces (baked)
FEATURE [Part::Feature] Clone001031  label="strutcap053"
  Placement = pos=(1780.84,-21.3342,896.949) rot=(0.871498,-0.474485,0.123916;1.43836rad)
  shape: bbox 24.48 x 32.39 x 22.88 mm, 19 faces (baked)
FEATURE [Part::Feature] Cylinder022  label="Cylinder006"
  Placement = pos=(1780.87,-21.342,896.969) rot=(0.871257,-0.475095,0.123269;1.43902rad)
  shape: bbox 404.7 x 961.7 x 161.3 mm, 3 faces (baked)
FEATURE [Part::Feature] Clone001032  label="strutcap054"
  Placement = pos=(1385.02,-979.035,1048.21) rot=(-0.930319,-0.067054,-0.360569;1.89034rad)
  shape: bbox 27.6 x 31.33 x 20.29 mm, 19 faces (baked)
FEATURE [Part::Feature] Clone001033  label="Hub-017"
  Placement = pos=(1367.82,-993.731,1044.96) rot=(0.270395,0.832171,-0.484126;1.1821rad)
  shape: bbox 46.31 x 51.62 x 50.16 mm, 28 faces (baked)
FEATURE [Part::Feature] Clone001036  label="strutcap057"
  Placement = pos=(1359.16,-1014.63,1048.21) rot=(0.830217,-0.556143,-0.038018;1.57228rad)
  shape: bbox 27.82 x 32.54 x 20 mm, 19 faces (baked)
FEATURE [Part::Feature] Clone001037  label="strutcap058"
  Placement = pos=(1373.71,-1011.61,1031.99) rot=(0.909326,-0.37369,0.182983;2.49398rad)
  shape: bbox 21.91 x 31.15 x 29.81 mm, 19 faces (baked)
FEATURE [Part::Feature] Clone001038  label="strutcap059"
  Placement = pos=(1386.64,-993.808,1031.99) rot=(0.962095,-0.192679,0.192997;3.57034rad)
  shape: bbox 28.43 x 23.66 x 30.86 mm, 19 faces (baked)
FEATURE [Part::Part2DObjectPython] Line054  # Draft 2D object (typed FeaturePython)
  ChamferSize = 0
  Closed = false
  End = (1902.16,-617.998,0)
  FilletRadius = 0
  Length = 1236.1
  MakeFace = true
  MapMode = 5
  Points = (2) [(1175.6,-1618.02,0),(1902.16,-617.998,0)]
  Start = (1175.6,-1618.02,0)
  Subdivisions = 0
FEATURE [Part::Part2DObjectPython] Line055  # Draft 2D object (typed FeaturePython)
  ChamferSize = 0
  Closed = false
  End = (1902.16,617.998,0)
  FilletRadius = 0
  Length = 1236
  MakeFace = true
  MapMode = 5
  Points = (2) [(1902.16,-617.998,0),(1902.16,617.998,0)]
  Start = (1902.16,-617.998,0)
  Subdivisions = 0
FEATURE [Part::Part2DObjectPython] Line056  # Draft 2D object (typed FeaturePython)
  ChamferSize = 0
  Closed = false
  End = (1376.39,-999.957,1051.5)
  FilletRadius = 0
  Length = 1236
  MakeFace = true
  MapMode = 5
  Points = (2) [(1051.49,1.3321e-09,1701.28),(1376.39,-999.957,1051.5)]
  Start = (1051.49,1.332e-09,1701.28)
  Subdivisions = 0
FEATURE [Part::Part2DObjectPython] Line057  # Draft 2D object (typed FeaturePython)
  ChamferSize = 0
  Closed = false
  End = (1902.16,-617.998,0)
  FilletRadius = 0
  Length = 1236.11
  MakeFace = true
  MapMode = 5
  Points = (2) [(1376.39,-999.957,1051.5),(1902.16,-617.998,0)]
  Start = (1376.39,-999.957,1051.5)
  Subdivisions = 0
FEATURE [Part::Part2DObjectPython] Line058  # Draft 2D object (typed FeaturePython)
  ChamferSize = 0
  Closed = false
  End = (1376.39,999.957,1051.5)
  FilletRadius = 0
  Length = 1236
  MakeFace = true
  MapMode = 5
  Points = (2) [(1051.49,1.3321e-09,1701.28),(1376.39,999.957,1051.5)]
  Start = (1051.49,1.332e-09,1701.28)
  Subdivisions = 0
FEATURE [Part::Part2DObjectPython] Line059  # Draft 2D object (typed FeaturePython)
  ChamferSize = 0
  Closed = false
  End = (1902.16,617.998,0)
  FilletRadius = 0
  Length = 1236.11
  MakeFace = true
  MapMode = 5
  Points = (2) [(1376.39,999.957,1051.5),(1902.16,617.998,0)]
  Start = (1376.39,999.957,1051.5)
  Subdivisions = 0
FEATURE [Part::Feature] Cylinder023  label="Varilla-B-modif-005"
  Placement = pos=(1891.94,625.428,20.4541) rot=(-0.256517,-0.683428,-0.683465;0.767356rad)
  shape: bbox 514.7 x 376.8 x 1017 mm, 3 faces (baked)
FEATURE [Part::Feature] Clone001039  label="strutcap060"
  Placement = pos=(1386.87,993.248,1032.31) rot=(0.963511,0.189033,0.189506;2.73838rad)
  shape: bbox 28.28 x 23.32 x 30.96 mm, 19 faces (baked)
FEATURE [Part::Feature] Clone001040  label="strutcap061"
  Placement = pos=(1892,626.262,19.0526) rot=(-0.586671,-0.615427,0.526371;0.557536rad)
  shape: bbox 24.41 x 24.08 x 32.46 mm, 19 faces (baked)
FEATURE [Part::Feature] Clone001041  label="strutcap062"
  Placement = pos=(1370.43,982.035,1064.4) rot=(0.652966,-0.542424,0.528594;1.20781rad)
  shape: bbox 22.88 x 30.45 x 29.86 mm, 19 faces (baked)
FEATURE [Part::Feature] Cylinder024  label="Varilla-B-modif-006"
  Placement = pos=(1057.35,20.059,1689.56) rot=(0.887762,0.32548,0.325486;3.92675rad)
  shape: bbox 322.6 x 967 x 634.3 mm, 3 faces (baked)
FEATURE [Part::Feature] Clone001042  label="strutcap063"
  Placement = pos=(1057.34,19.1988,1690.32) rot=(0.882765,0.34052,0.323687;3.95983rad)
  shape: bbox 24.7 x 32.04 x 26.61 mm, 19 faces (baked)
FEATURE [Part::Feature] Cylinder025  label="Varilla-B-modif-007"
  Placement = pos=(1386.68,-992.502,1030.9) rot=(0.93165,0.256925,0.256939;3.33301rad)
  shape: bbox 514.9 x 375.8 x 1017 mm, 3 faces (baked)
FEATURE [Part::Feature] Clone001043  label="strutcap064"
  Placement = pos=(1892.07,-626.034,19.189) rot=(0.64134,-0.542546,-0.542518;0.709896rad)
  shape: bbox 25.5 x 26.02 x 32.03 mm, 19 faces (baked)
FEATURE [Part::Feature] Clone001044  label="strutcap065"
  Placement = pos=(1370.47,-982.061,1064.43) rot=(-0.67332,-0.525087,-0.520503;1.20241rad)
  shape: bbox 22.54 x 30.53 x 29.82 mm, 19 faces (baked)
FEATURE [Part::Feature] Clone001045  label="strutcap066"
  Placement = pos=(1057.56,-19.0526,1690.18) rot=(0.887841,-0.325204,0.325548;2.35642rad)
  shape: bbox 25.29 x 31.82 x 26.9 mm, 19 faces (baked)
FEATURE [Part::Feature] Cylinder027  label="Varilla-B-modif-009"
  Placement = pos=(1370.47,-982.061,1064.43) rot=(-0.669151,-0.525446,-0.525494;1.2188rad)
  shape: bbox 322.1 x 967.7 x 633.5 mm, 3 faces (baked)
FEATURE [Part::Part2DObjectPython] Line060  # Draft 2D object (typed FeaturePython)
  ChamferSize = 0
  Closed = false
  End = (324.929,1000.03,1701.28)
  FilletRadius = 0
  Length = 1236.1
  MakeFace = true
  MapMode = 5
  Points = (2) [(-850.675,618.052,1701.28),(324.929,1000.03,1701.28)]
  Start = (-850.675,618.052,1701.28)
  Subdivisions = 0
FEATURE [Part::Feature] Clone001047  label="strutcap068"
  Placement = pos=(302.894,993.894,1701.75) rot=(-0.095426,-0.931982,0.349719;1.72702rad)
  shape: bbox 31.97 x 22.84 x 20.72 mm, 19 faces (baked)
FEATURE [Part::Feature] Clone001049  label="strutcap070"
  Placement = pos=(-17.7986,12.9312,1993.75) rot=(-0.300922,-0.926155,-0.227341;1.92055rad)
  shape: bbox 31.35 x 28.31 x 22.68 mm, 19 faces (baked)
FEATURE [Part::Feature] Cylinder  label="Cylinder007"
  Placement = pos=(-17.7986,12.9312,1993.75) rot=(-0.842809,-0.429437,0.324432;2.00762rad)
  shape: bbox 821.2 x 600.3 x 295.8 mm, 3 faces (baked)
FEATURE [Part::Feature] Clone001050  label="Hub-018"
  Placement = pos=(-845.385,614.197,1690.69) rot=(-0.229479,0.149024,0.961837;3.04087rad)
  shape: bbox 52.89 x 52.48 x 37.22 mm, 28 faces (baked)
FEATURE [Part::Feature] Clone001051  label="strutcap071"
  Placement = pos=(-832.882,605.113,1707.53) rot=(0.591556,-0.192206,0.783019;2.64333rad)
  shape: bbox 30.27 x 27.49 x 25.37 mm, 19 faces (baked)
FEATURE [Part::Feature] Clone001052  label="strutcap072"
  Placement = pos=(-829.253,626.027,1701.75) rot=(0.656731,0.274649,0.702334;3.0586rad)
  shape: bbox 31.36 x 25.66 x 20.75 mm, 19 faces (baked)
FEATURE [Part::Feature] Clone001053  label="strutcap073"
  Placement = pos=(-844.393,637.027,1690.18) rot=(0.558841,0.681764,0.472117;3.47389rad)
  shape: bbox 22.99 x 32.33 x 26.68 mm, 19 faces (baked)
FEATURE [Part::Feature] Clone001054  label="strutcap074"
  Placement = pos=(-863.162,627.113,1684.4) rot=(0.306814,0.944291,0.119074;3.84415rad)
  shape: bbox 29.74 x 26.84 x 29.82 mm, 19 faces (baked)
FEATURE [Part::Feature] Clone001055  label="strutcap075"
  Placement = pos=(-866.791,606.199,1690.18) rot=(-0.037385,0.949845,-0.310478;3.97036rad)
  shape: bbox 31.57 x 26.83 x 26.72 mm, 19 faces (baked)
FEATURE [Part::Feature] Clone001056  label="strutcap076"
  Placement = pos=(-851.651,595.199,1701.75) rot=(-0.384951,0.662639,-0.642435;3.89838rad)
  shape: bbox 20.26 x 30.22 x 20.72 mm, 19 faces (baked)
FEATURE [Part::Feature] Cylinder028  label="Varilla-B-modif-010"
  Placement = pos=(-827.741,626.518,1701.75) rot=(0.456965,0.628961,0.628961;2.28433rad)
  shape: bbox 1134 x 376.9 x 10 mm, 3 faces (baked)
FEATURE [Part::Part2DObjectPython] Line061  # Draft 2D object (typed FeaturePython)
  ChamferSize = 0
  Closed = false
  End = (-850.675,-618.052,1701.28)
  FilletRadius = 0
  Length = 1236.1
  MakeFace = true
  MapMode = 5
  Points = (2) [(-850.675,618.052,1701.28),(-850.675,-618.052,1701.28)]
  Start = (-850.675,618.052,1701.28)
  Subdivisions = 0
FEATURE [Part::Part2DObjectPython] Line062  # Draft 2D object (typed FeaturePython)
  ChamferSize = 0
  Closed = false
  End = (324.937,-1000.03,1701.28)
  FilletRadius = 0
  Length = 1236.11
  MakeFace = true
  MapMode = 5
  Points = (2) [(-850.675,-618.052,1701.28),(324.937,-1000.03,1701.28)]
  Start = (-850.675,-618.052,1701.28)
  Subdivisions = 0
FEATURE [Part::Part2DObjectPython] Line063  # Draft 2D object (typed FeaturePython)
  ChamferSize = 0
  Closed = false
  End = (1051.49,1.332e-09,1701.28)
  FilletRadius = 0
  Length = 1236.1
  MakeFace = true
  MapMode = 5
  Points = (2) [(324.929,1000.03,1701.28),(1051.49,1.3321e-09,1701.28)]
  Start = (324.929,1000.03,1701.28)
  Subdivisions = 0
FEATURE [Part::Part2DObjectPython] Line064  # Draft 2D object (typed FeaturePython)
  ChamferSize = 0
  Closed = false
  End = (324.937,-1000.03,1701.28)
  FilletRadius = 0
  Length = 1236.1
  MakeFace = true
  MapMode = 5
  Points = (2) [(1051.49,1.3321e-09,1701.28),(324.937,-1000.03,1701.28)]
  Start = (1051.49,1.332e-09,1701.28)
  Subdivisions = 0
FEATURE [Part::Feature] Clone001057  label="strutcap077"
  Placement = pos=(-17.7984,-12.9315,1993.75) rot=(0.300929,-0.926151,0.227346;1.92056rad)
  shape: bbox 31.35 x 28.31 x 22.68 mm, 19 faces (baked)
FEATURE [Part::Feature] Cylinder029  label="Cylinder008"
  Placement = pos=(-17.7984,-12.9315,1993.75) rot=(0.376611,0.739148,-0.558413;3.69599rad)
  shape: bbox 821.2 x 600.3 x 295.8 mm, 3 faces (baked)
FEATURE [Part::Feature] Clone001058  label="Hub-019"
  Placement = pos=(-845.374,-614.211,1690.69) rot=(0.320391,0.016792,-0.947137;2.03872rad)
  shape: bbox 52.89 x 52.48 x 37.22 mm, 28 faces (baked)
FEATURE [Part::Feature] Clone001059  label="strutcap078"
  Placement = pos=(-851.64,-595.214,1701.75) rot=(0.399329,0.656651,0.639801;3.91882rad)
  shape: bbox 20.03 x 30.19 x 20.75 mm, 19 faces (baked)
FEATURE [Part::Feature] Clone001060  label="strutcap079"
  Placement = pos=(-866.78,-606.214,1690.18) rot=(0.055489,0.9504,0.306039;3.98098rad)
  shape: bbox 31.55 x 26.91 x 26.68 mm, 19 faces (baked)
FEATURE [Part::Feature] Clone001061  label="strutcap080"
  Placement = pos=(-832.872,-605.127,1707.53) rot=(0.591556,0.192211,0.783018;3.63986rad)
  shape: bbox 30.27 x 27.49 x 25.37 mm, 19 faces (baked)
FEATURE [Part::Feature] Clone001062  label="strutcap081"
  Placement = pos=(-829.243,-626.041,1701.75) rot=(0.652221,-0.288292,0.701067;3.2457rad)
  shape: bbox 31.36 x 25.86 x 20.72 mm, 19 faces (baked)
FEATURE [Part::Feature] Clone001063  label="strutcap082"
  Placement = pos=(-844.383,-637.041,1690.18) rot=(-0.545652,0.692057,-0.472568;3.4603rad)
  shape: bbox 22.9 x 32.27 x 26.72 mm, 19 faces (baked)
FEATURE [Part::Feature] Clone001064  label="strutcap083"
  Placement = pos=(-863.151,-627.127,1684.4) rot=(-0.306822,0.944288,-0.119077;3.84415rad)
  shape: bbox 29.74 x 26.84 x 29.82 mm, 19 faces (baked)
FEATURE [Part::Feature] Cylinder030  label="Varilla-B-modif-011"
  Placement = pos=(-851.641,-593.624,1701.75) rot=(-1e-06,0.707107,0.707107;3.1416rad)
  shape: bbox 10.01 x 1189 x 10 mm, 3 faces (baked)
FEATURE [Part::Feature] Clone001065  label="strutcap084"
  Placement = pos=(6.79873,-20.9232,1993.75) rot=(0.690296,-0.501521,0.521506;2.41724rad)
  shape: bbox 23.54 x 32.47 x 22.68 mm, 19 faces (baked)
FEATURE [App::DocumentObjectGroup] Group011  label="Clave"
  Group = -> [Clone001004,Clone,Clone001065,Clone001057,Clone001049,Clone001015]
FEATURE [Part::Feature] Cylinder031  label="Cylinder009"
  Placement = pos=(6.79873,-20.9232,1993.75) rot=(-0.125384,0.791599,-0.598038;2.95271rad)
  shape: bbox 320.8 x 962 x 295.8 mm, 3 faces (baked)
FEATURE [Part::Feature] Clone001066  label="Hub-020"
  Placement = pos=(322.923,-993.798,1690.69) rot=(0.482777,0.390952,-0.783634;0.910971rad)
  shape: bbox 55.11 x 51.63 x 37.22 mm, 28 faces (baked)
FEATURE [Part::Feature] Clone001067  label="strutcap085"
  Placement = pos=(318.147,-979.1,1707.53) rot=(-0.46391,-0.638529,-0.614059;1.7382rad)
  shape: bbox 23.11 x 31.33 x 25.37 mm, 19 faces (baked)
FEATURE [Part::Feature] Clone001068  label="strutcap086"
  Placement = pos=(302.919,-993.887,1701.75) rot=(0.077008,-0.937624,-0.339015;1.71438rad)
  shape: bbox 31.95 x 22.93 x 20.75 mm, 19 faces (baked)
FEATURE [Part::Feature] Clone001069  label="strutcap087"
  Placement = pos=(308.702,-1011.68,1690.18) rot=(-0.539571,0.841799,-0.015424;4.17481rad)
  shape: bbox 29.86 x 29.01 x 26.68 mm, 19 faces (baked)
FEATURE [Part::Feature] Clone001070  label="strutcap088"
  Placement = pos=(329.714,-1014.7,1684.4) rot=(0.771869,-0.560786,0.299561;2.713rad)
  shape: bbox 22.65 x 31.16 x 29.82 mm, 19 faces (baked)
FEATURE [Part::Feature] Clone001071  label="strutcap089"
  Placement = pos=(344.942,-999.909,1690.18) rot=(0.846307,-0.244693,0.47317;3.42288rad)
  shape: bbox 32.71 x 20 x 26.83 mm, 19 faces (baked)
FEATURE [Part::Feature] Clone001072  label="strutcap090"
  Placement = pos=(339.159,-982.111,1701.75) rot=(0.781158,0.168237,0.601239;4.08322rad)
  shape: bbox 29.92 x 30.42 x 20.72 mm, 19 faces (baked)
FEATURE [Part::Feature] Cylinder032  label="Varilla-B-modif-012"
  Placement = pos=(301.407,-993.395,1701.75) rot=(-0.456971,0.628958,0.628958;3.99886rad)
  shape: bbox 1134 x 376.9 x 10 mm, 3 faces (baked)
FEATURE [Part::Feature] Cylinder033  label="Varilla-B-modif-013"
  Placement = pos=(1037.92,-20.3126,1701.75) rot=(0.908667,-0.295233,-0.295233;1.66643rad)
  shape: bbox 706.8 x 967.7 x 10 mm, 3 faces (baked)
FEATURE [Part::Part2DObjectPython] Line065  # Draft 2D object (typed FeaturePython)
  ChamferSize = 0
  Closed = false
  End = (1376.39,-999.957,1051.5)
  FilletRadius = 0
  Length = 1236.03
  MakeFace = true
  MapMode = 5
  Points = (2) [(324.937,-1000.03,1701.28),(1376.39,-999.957,1051.5)]
  Start = (324.937,-1000.03,1701.28)
  Subdivisions = 0
FEATURE [Part::Feature] Cylinder034  label="Varilla-B-modif-014"
  Placement = pos=(1357.36,-1000.76,1064.14) rot=(0.086928,-0.983946,-0.155865;1.03106rad)
  shape: bbox 1017 x 10.03 x 633.5 mm, 3 faces (baked)
FEATURE [Part::Feature] Clone001073  label="strutcap091"
  Placement = pos=(1357.54,-999.86,1064.43) rot=(0.250583,-0.868506,-0.427675;1.13881rad)
  shape: bbox 30.96 x 20.1 x 29.71 mm, 19 faces (baked)
FEATURE [Part::Feature] Cylinder035  label="Cylinder010"
  Placement = pos=(329.697,1014.7,1684.4) rot=(0.985873,-0.156147,0.060603;3.87249rad)
  shape: bbox 228.1 x 679.5 x 779.7 mm, 3 faces (baked)
FEATURE [Part::Feature] Cylinder036  label="Varilla-B-modif-015"
  Placement = pos=(1357.49,999.919,1064.43) rot=(-0.245397,-0.863791,0.440052;1.14636rad)
  shape: bbox 1017 x 10.05 x 633.5 mm, 3 faces (baked)
FEATURE [Part::Feature] Cylinder037  label="Varilla-B-modif-016"
  Placement = pos=(307.663,1011.8,1689.56) rot=(0.557122,0.830163,0.021082;4.15722rad)
  shape: bbox 824.6 x 603.3 x 634.3 mm, 3 faces (baked)
FEATURE [Part::Feature] Clone001074  label="strutcap092"
  Placement = pos=(344.925,999.915,1690.18) rot=(0.847741,0.241212,0.472389;2.87537rad)
  shape: bbox 32.7 x 20 x 26.9 mm, 19 faces (baked)
FEATURE [Part::Feature] Clone001075  label="strutcap093"
  Placement = pos=(329.697,1014.7,1684.4) rot=(0.771865,0.560793,0.299559;3.57019rad)
  shape: bbox 22.65 x 31.16 x 29.82 mm, 19 faces (baked)
FEATURE [Part::Feature] Clone001076  label="strutcap094"
  Placement = pos=(308.478,1011.53,1690.32) rot=(0.543251,0.839537,0.007414;4.18045rad)
  shape: bbox 29.9 x 28.94 x 26.61 mm, 19 faces (baked)
FEATURE [Part::Feature] Clone001077  label="strutcap095"
  Placement = pos=(1357.49,999.919,1064.43) rot=(-0.246268,-0.855952,0.454641;1.14624rad)
  shape: bbox 30.92 x 20 x 29.82 mm, 19 faces (baked)
FEATURE [Part::Feature] Cylinder038  label="Varilla-B-modif-017"
  Placement = pos=(-867.207,605.268,1689.56) rot=(-0.035573,0.954465,-0.296196;3.97386rad)
  shape: bbox 825.4 x 602.3 x 634.3 mm, 3 faces (baked)
FEATURE [Part::Feature] Cylinder039  label="Cylinder011"
  Placement = pos=(-863.157,627.12,1684.4) rot=(0.877489,0.447103,-0.173528;3.79809rad)
  shape: bbox 579.9 x 424.4 x 779.7 mm, 3 faces (baked)
FEATURE [Part::Feature] Cylinder040  label="Varilla-B-modif-018"
  Placement = pos=(-531.491,1600.04,1064.43) rot=(0.199138,-0.542979,0.815793;2.00203rad)
  shape: bbox 322.2 x 967.7 x 633.5 mm, 3 faces (baked)
FEATURE [Part::Feature] Cylinder041  label="Varilla-B-modif-019"
  Placement = pos=(-1685.97,-11.0365,1064.43) rot=(0.404604,-0.271467,0.87327;3.07625rad)
  shape: bbox 825.4 x 603.1 x 633.5 mm, 3 faces (baked)
FEATURE [Part::Feature] Cylinder042  label="Cylinder012"
  Placement = pos=(-863.157,-627.12,1684.4) rot=(0.42906,0.842077,-0.326825;3.47161rad)
  shape: bbox 579.9 x 424.4 x 779.7 mm, 3 faces (baked)
FEATURE [Part::Feature] Cylinder043  label="Varilla-B-modif-020"
  Placement = pos=(-843.626,-637.725,1689.56) rot=(-0.547223,0.697036,-0.463345;3.47876rad)
  shape: bbox 321.4 x 967.4 x 634.3 mm, 3 faces (baked)
FEATURE [Part::Feature] Cylinder044  label="Varilla-B-modif-021"
  Placement = pos=(-510.484,-1606.87,1064.43) rot=(0.55703,0.020822,0.830232;4.15797rad)
  shape: bbox 825.4 x 603 x 633.5 mm, 3 faces (baked)
FEATURE [Part::Feature] Cylinder045  label="Cylinder013"
  Placement = pos=(329.705,-1014.7,1684.4) rot=(-0.146074,0.922248,-0.35794;3.02833rad)
  shape: bbox 228.1 x 679.5 x 779.7 mm, 3 faces (baked)
FEATURE [Part::Feature] Cylinder046  label="Cylinder014"
  Placement = pos=(540.281,1707.78,876.414) rot=(0.752998,0.648404,-0.1121;3.71301rad)
  shape: bbox 538.6 x 295.9 x 862.3 mm, 3 faces (baked)
FEATURE [Part::Feature] Cylinder047  label="Cylinder015"
  Placement = pos=(565.816,1699.57,875.771) rot=(0.764557,0.607953,0.214116;2.70375rad)
  shape: bbox 604.8 x 89.65 x 862.6 mm, 3 faces (baked)
FEATURE [Part::Feature] Cylinder048  label="Varilla-B-modif-022"
  Placement = pos=(22.9176,1992.61,-2.89e-13) rot=(0.697446,0.506739,0.506739;1.92357rad)
  shape: bbox 1134 x 376.8 x 10 mm, 3 faces (baked)
FEATURE [Part::Feature] Cylinder049  label="Cylinder016"
  Placement = pos=(-1457.24,1041.57,876.414) rot=(0.221853,0.940826,-0.256178;3.47269rad)
  shape: bbox 445.1 x 424.7 x 862.3 mm, 3 faces (baked)
FEATURE [Part::Feature] Cylinder050  label="Varilla-B-modif-023"
  Placement = pos=(-1888,637.545,-2.89e-13) rot=(0.223909,0.689153,0.689153;2.70104rad)
  shape: bbox 706.8 x 967.7 x 10 mm, 3 faces (baked)
FEATURE [Part::Feature] Cylinder051  label="Cylinder017"
  Placement = pos=(-1441.54,1063.32,875.771) rot=(0.255317,0.92006,0.297158;3.03584rad)
  shape: bbox 269.8 x 551.3 x 862.6 mm, 3 faces (baked)
FEATURE [Part::Feature] Cylinder052  label="Varilla-B-modif-024"
  Placement = pos=(-1189.77,-1598.58,-2.89e-13) rot=(-0.223929,0.68915,0.68915;3.58218rad)
  shape: bbox 706.9 x 967.6 x 10 mm, 3 faces (baked)
FEATURE [Part::Feature] Cylinder053  label="Cylinder018"
  Placement = pos=(-1440.9,-1064.05,876.414) rot=(-0.368456,0.879459,-0.301316;3.11119rad)
  shape: bbox 270.1 x 551.7 x 862.3 mm, 3 faces (baked)
FEATURE [Part::Feature] Cylinder054  label="Cylinder019"
  Placement = pos=(-1456.73,-1042.4,875.771) rot=(-0.336706,0.901009,0.273516;3.40569rad)
  shape: bbox 444.9 x 424.3 x 862.6 mm, 3 faces (baked)
FEATURE [Part::Feature] Cylinder055  label="Cylinder020"
  Placement = pos=(541.239,-1707.55,875.771) rot=(0.824708,-0.546051,-0.147262;2.60334rad)
  shape: bbox 538.1 x 295.8 x 862.6 mm, 3 faces (baked)
FEATURE [Part::Feature] Cylinder056  label="Varilla-B-modif-025"
  Placement = pos=(1152.7,-1625.51,0) rot=(0.69747,-0.506723,-0.506723;1.92354rad)
  shape: bbox 1134 x 376.9 x 10 mm, 3 faces (baked)
FEATURE [Part::Feature] Cylinder057  label="Cylinder021"
  Placement = pos=(566.724,-1699.19,876.414) rot=(0.829948,-0.503984,0.239135;3.52267rad)
  shape: bbox 605.2 x 89.84 x 862.3 mm, 3 faces (baked)
FEATURE [Part::Feature] Clone001078  label="strutcap096"
  Placement = pos=(530.378,1699.18,898.82) rot=(-0.414259,-0.732085,0.540778;1.78299rad)
  shape: bbox 30.96 x 20.14 x 22.38 mm, 19 faces (baked)
FEATURE [Part::Feature] Clone001079  label="strutcap097"
  Placement = pos=(540.273,1707.74,876.408) rot=(0.753174,0.648286,-0.111595;3.71391rad)
  shape: bbox 26.59 x 25.55 x 30.67 mm, 19 faces (baked)
FEATURE [Part::Feature] Clone001080  label="strutcap098"
  Placement = pos=(565.808,1699.53,875.769) rot=(0.764338,0.608049,0.214624;2.70459rad)
  shape: bbox 28.6 x 20 x 30.68 mm, 19 faces (baked)
FEATURE [Part::Feature] Clone001081  label="strutcap099"
  Placement = pos=(570.601,1687.09,896.949) rot=(0.782815,0.102142,0.613814;1.95118rad)
  shape: bbox 32 x 28.57 x 22.88 mm, 19 faces (baked)
FEATURE [Part::Feature] Clone001082  label="strutcap100"
  Placement = pos=(548.01,1686.6,911.365) rot=(0.323892,-0.445799,0.83448;1.43273rad)
  shape: bbox 21.5 x 28.59 x 31.71 mm, 19 faces (baked)
FEATURE [Part::Feature] Clone001083  label="Hub5-01-clave004"
  Placement = pos=(549.337,1690.68,888.915) rot=(0.403006,0.403003,0.82169;3.9346rad)
  shape: bbox 54.11 x 37.29 x 51.33 mm, 25 faces (baked)
FEATURE [Part::Feature] Clone001084  label="Hub5-01-clave005"
  Placement = pos=(-1438.18,1044.9,888.915) rot=(-0.126077,-0.795998,-0.592023;1.42128rad)
  shape: bbox 45.2 x 49.91 x 51.33 mm, 25 faces (baked)
FEATURE [Part::Feature] Clone001085  label="strutcap101"
  Placement = pos=(-1457.21,1041.55,876.408) rot=(0.222054,0.940813,-0.256052;3.47399rad)
  shape: bbox 28.2 x 24.81 x 30.67 mm, 19 faces (baked)
FEATURE [Part::Feature] Clone001086  label="strutcap102"
  Placement = pos=(-1441.51,1063.3,875.769) rot=(0.255103,0.920065,0.297325;3.03711rad)
  shape: bbox 22.21 x 29.03 x 30.68 mm, 19 faces (baked)
FEATURE [Part::Feature] Clone001087  label="strutcap103"
  Placement = pos=(-1428.19,1064.01,896.949) rot=(0.480485,0.454913,0.749792;2.83064rad)
  shape: bbox 30.89 x 29.5 x 22.88 mm, 19 faces (baked)
FEATURE [Part::Feature] Clone001088  label="strutcap104"
  Placement = pos=(-1434.71,1042.38,911.365) rot=(0.359362,-0.116764,0.925865;2.55715rad)
  shape: bbox 27.2 x 24.82 x 31.71 mm, 19 faces (baked)
FEATURE [Part::Feature] Clone001089  label="strutcap105"
  Placement = pos=(-1452.12,1029.49,898.82) rot=(0.076698,-0.673574,0.735129;2.61355rad)
  shape: bbox 25.23 x 31.29 x 22.38 mm, 19 faces (baked)
FEATURE [Part::Feature] Clone001090  label="Hub5-01-clave006"
  Placement = pos=(-1438.18,-1044.9,888.915) rot=(0.440106,-0.863765,0.245392;1.14634rad)
  shape: bbox 45.2 x 49.91 x 51.33 mm, 25 faces (baked)
FEATURE [Part::Feature] Clone001091  label="strutcap106"
  Placement = pos=(-1456.71,-1042.38,875.769) rot=(-0.336923,0.900992,0.273307;3.40693rad)
  shape: bbox 28.13 x 24.8 x 30.68 mm, 19 faces (baked)
FEATURE [Part::Feature] Clone001092  label="strutcap107"
  Placement = pos=(-1453.27,-1029.49,896.949) rot=(0.126083,0.675935,0.726096;3.77224rad)
  shape: bbox 25.11 x 31.29 x 22.88 mm, 19 faces (baked)
FEATURE [Part::Feature] Clone001093  label="strutcap108"
  Placement = pos=(-1434.71,-1042.38,911.365) rot=(0.359362,0.116764,0.925865;3.72603rad)
  shape: bbox 27.2 x 24.82 x 31.71 mm, 19 faces (baked)
FEATURE [Part::Feature] Clone001094  label="strutcap109"
  Placement = pos=(-1427.84,-1062.91,898.82) rot=(0.451787,-0.493106,0.743461;3.55656rad)
  shape: bbox 30.89 x 29.64 x 22.38 mm, 19 faces (baked)
FEATURE [Part::Feature] Clone001095  label="strutcap110"
  Placement = pos=(-1440.88,-1064.03,876.408) rot=(-0.368245,0.879462,-0.301567;3.11241rad)
  shape: bbox 22.22 x 29.51 x 30.67 mm, 19 faces (baked)
FEATURE [Part::Feature] Clone001096  label="Hub5-01-clave007"
  Placement = pos=(549.351,-1690.68,888.915) rot=(0.58635,-0.29876,0.752952;1.85083rad)
  shape: bbox 54.11 x 37.29 x 51.33 mm, 25 faces (baked)
FEATURE [Part::Feature] Clone001097  label="strutcap111"
  Placement = pos=(530.035,-1700.27,896.949) rot=(0.372241,-0.78273,-0.49877;1.70887rad)
  shape: bbox 30.96 x 20.06 x 22.88 mm, 19 faces (baked)
FEATURE [Part::Feature] Clone001098  label="strutcap112"
  Placement = pos=(541.226,-1707.52,875.769) rot=(0.824895,-0.545917,-0.146708;2.60259rad)
  shape: bbox 26.57 x 25.89 x 30.68 mm, 19 faces (baked)
FEATURE [Part::Feature] Clone001099  label="strutcap113"
  Placement = pos=(548.024,-1686.6,911.365) rot=(-0.323892,-0.445802,-0.834479;1.43272rad)
  shape: bbox 21.5 x 28.59 x 31.71 mm, 19 faces (baked)
FEATURE [Part::Feature] Clone001100  label="strutcap114"
  Placement = pos=(569.68,-1686.41,898.82) rot=(-0.797368,0.162279,-0.581265;1.86885rad)
  shape: bbox 32.15 x 28.57 x 22.38 mm, 19 faces (baked)
FEATURE [Part::Feature] Clone001101  label="strutcap115"
  Placement = pos=(566.711,-1699.15,876.408) rot=(0.829728,-0.504084,0.239691;3.52197rad)
  shape: bbox 29.43 x 20.13 x 30.67 mm, 19 faces (baked)
FEATURE [Part::Feature] Clone001102  label="Hub-021"
  Placement = pos=(-522.419,1607.96,1044.94) rot=(-0.404151,-0.556253,-0.726117;1.57141rad)
  shape: bbox 54.14 x 40.13 x 50.11 mm, 28 faces (baked)
FEATURE [Part::Feature] Clone001105  label="strutcap118"
  Placement = pos=(-516.067,1625.93,1032.31) rot=(0.655766,0.705688,0.268283;3.03581rad)
  shape: bbox 25.3 x 25.97 x 30.96 mm, 19 faces (baked)
FEATURE [Part::Feature] Clone001106  label="strutcap119"
  Placement = pos=(-503.124,1619.77,1048.2) rot=(0.67398,0.417938,0.609162;2.53046rad)
  shape: bbox 30.99 x 22.33 x 20.3 mm, 19 faces (baked)
FEATURE [Part::Feature] Clone001107  label="strutcap120"
  Placement = pos=(-510.484,1606.82,1064.4) rot=(0.551632,-0.035834,0.833318;2.11859rad)
  shape: bbox 28.95 x 26.75 x 29.86 mm, 19 faces (baked)
FEATURE [Part::Feature] Clone001108  label="strutcap121"
  Placement = pos=(-531.49,1600.04,1064.43) rot=(0.195018,-0.537301,0.820534;2.01296rad)
  shape: bbox 24.18 x 30.56 x 29.82 mm, 19 faces (baked)
FEATURE [Part::Feature] Clone001109  label="Hub-022"
  Placement = pos=(-1690.7,0.0372864,1044.94) rot=(-1.1e-05,-1,-2e-05;1.01578rad)
  shape: bbox 37.43 x 53.16 x 50.11 mm, 28 faces (baked)
FEATURE [Part::Feature] Clone001111  label="strutcap123"
  Placement = pos=(-1705.82,11.6304,1032.31) rot=(0.116339,0.961371,0.249462;3.3715rad)
  shape: bbox 23.88 x 27.32 x 30.96 mm, 19 faces (baked)
FEATURE [Part::Feature] Clone001112  label="strutcap124"
  Placement = pos=(-1695.97,22.0374,1048.2) rot=(0.287109,0.703654,0.649954;3.33809rad)
  shape: bbox 21.94 x 32.05 x 20.3 mm, 19 faces (baked)
FEATURE [Part::Feature] Clone001113  label="strutcap125"
  Placement = pos=(-1685.93,11.0372,1064.4) rot=(0.407724,0.257586,0.87602;3.20384rad)
  shape: bbox 29.33 x 26.91 x 29.86 mm, 19 faces (baked)
FEATURE [Part::Feature] Clone001114  label="strutcap126"
  Placement = pos=(-1685.97,-11.0364,1064.43) rot=(0.40029,-0.270519,0.87555;3.09124rad)
  shape: bbox 29.19 x 27.26 x 29.82 mm, 19 faces (baked)
FEATURE [Part::Feature] Clone001116  label="Hub-023"
  Placement = pos=(-522.49,-1607.94,1044.94) rot=(0.404145,-0.55627,0.726106;1.57137rad)
  shape: bbox 54.14 x 40.13 x 50.11 mm, 28 faces (baked)
FEATURE [Part::Feature] Clone001117  label="strutcap128"
  Placement = pos=(-510.498,-1606.87,1064.43) rot=(0.555204,0.018892,0.8315;4.17521rad)
  shape: bbox 29.12 x 26.51 x 29.82 mm, 19 faces (baked)
FEATURE [Part::Feature] Clone001118  label="strutcap129"
  Placement = pos=(-531.478,-1600,1064.4) rot=(-0.211892,-0.532008,-0.819798;2.00111rad)
  shape: bbox 23.74 x 30.6 x 29.86 mm, 19 faces (baked)
FEATURE [Part::Feature] Clone001119  label="strutcap130"
  Placement = pos=(-545.042,-1606.15,1048.2) rot=(-0.203171,0.82696,0.52427;4.09656rad)
  shape: bbox 32.67 x 26.78 x 20.3 mm, 19 faces (baked)
FEATURE [Part::Feature] Clone001120  label="strutcap131"
  Placement = pos=(-538.189,-1618.74,1032.31) rot=(-0.481748,0.865531,0.13702;3.62315rad)
  shape: bbox 28.95 x 20.82 x 30.96 mm, 19 faces (baked)
FEATURE [Part::Feature] Cylinder058  label="Cylinder022"
  Placement = pos=(530.378,1699.21,898.834) rot=(-0.413717,-0.732343,0.540844;1.78399rad)
  shape: bbox 1035 x 89.07 x 159.4 mm, 3 faces (baked)
FEATURE [Part::Feature] Cylinder059  label="Cylinder023"
  Placement = pos=(570.617,1687.11,896.969) rot=(0.783276,0.101681,0.613303;1.95105rad)
  shape: bbox 795.2 x 679.7 x 161.3 mm, 3 faces (baked)
FEATURE [Part::Feature] Cylinder060  label="Varilla-B-modif-026"
  Placement = pos=(1372.43,1012.12,1030.9) rot=(0.616123,0.772286,0.154811;3.60091rad)
  shape: bbox 201.9 x 602.9 x 1017 mm, 3 faces (baked)
FEATURE [Part::Feature] Clone001123  label="strutcap134"
  Placement = pos=(1359.16,1014.63,1048.2) rot=(-0.756432,-0.638991,0.139644;1.73831rad)
  shape: bbox 30 x 31.16 x 20.3 mm, 19 faces (baked)
FEATURE [Part::Feature] Clone001124  label="strutcap135"
  Placement = pos=(1373.75,1011.64,1032.01) rot=(0.909322,0.414351,0.038035;3.6661rad)
  shape: bbox 20.28 x 29.06 x 31.05 mm, 19 faces (baked)
FEATURE [Part::Feature] Clone001125  label="Hub-024"
  Placement = pos=(1167.88,1607.21,-5e-15) rot=(-0.413351,0.811346,0.413351;1.77835rad)
  shape: bbox 48.34 x 39.86 x 55.6 mm, 28 faces (baked)
FEATURE [Part::Feature] Clone001126  label="strutcap136"
  Placement = pos=(1162.63,1618.69,19.0526) rot=(-0.354648,-0.474559,0.805617;1.14619rad)
  shape: bbox 28.01 x 22.72 x 31.69 mm, 19 faces (baked)
FEATURE [Part::Feature] Clone001127  label="strutcap137"
  Placement = pos=(1153.73,1625.15,0) rot=(-0.697483,-0.506713,0.506713;1.92352rad)
  shape: bbox 31.34 x 25.98 x 20 mm, 19 faces (baked)
FEATURE [Part::Feature] Clone001128  label="strutcap138"
  Placement = pos=(1180.54,1607.1,19.8831) rot=(0.632762,0.03188,0.77369;0.99253rad)
  shape: bbox 25.27 x 26.79 x 31.62 mm, 19 faces (baked)
FEATURE [Part::Feature] Clone001129  label="strutcap139"
  Placement = pos=(1189.16,1599.52,-2.5e-14) rot=(0.908302,0.295794,0.295794;1.66683rad)
  shape: bbox 30.1 x 30.58 x 20 mm, 19 faces (baked)
FEATURE [Part::Feature] Cylinder061  label="Varilla-B-modif-027"
  Placement = pos=(1189.84,1598.52,-2.89e-13) rot=(0.908667,0.295233,0.295233;1.66643rad)
  shape: bbox 706.8 x 967.7 x 10 mm, 3 faces (baked)
FEATURE [Part::Feature] Cylinder062  label="Varilla-B-modif-028"
  Placement = pos=(-538.473,1618.02,1030.9) rot=(0.045055,0.998909,-0.012317;3.69415rad)
  shape: bbox 633 x 11.04 x 1017 mm, 3 faces (baked)
FEATURE [Part::Feature] Cylinder063  label="Varilla-B-modif-029"
  Placement = pos=(-10.1769,1992.61,20.4541) rot=(0.167218,-0.60597,0.777714;0.899398rad)
  shape: bbox 514.7 x 376.9 x 1017 mm, 3 faces (baked)
FEATURE [Part::Feature] Cylinder064  label="Cylinder024"
  Placement = pos=(-1428.21,1064.04,896.969) rot=(0.481026,0.454827,0.749497;2.83001rad)
  shape: bbox 888.2 x 550.9 x 161.3 mm, 3 faces (baked)
FEATURE [Part::Feature] Clone001130  label="strutcap140"
  Placement = pos=(-544.971,1606.18,1048.2) rot=(0.203272,0.826904,-0.52432;4.09647rad)
  shape: bbox 32.67 x 26.78 x 20.3 mm, 19 faces (baked)
FEATURE [Part::Feature] Clone001131  label="strutcap141"
  Placement = pos=(-537.612,1619.12,1032.01) rot=(0.488533,0.863387,-0.126091;3.6085rad)
  shape: bbox 28.61 x 21.1 x 31.05 mm, 19 faces (baked)
FEATURE [Part::Feature] Cylinder065  label="Cylinder025"
  Placement = pos=(-1453.3,-1029.5,896.969) rot=(0.126564,0.676057,0.725898;3.77131rad)
  shape: bbox 252.7 x 1010 x 161.3 mm, 3 faces (baked)
FEATURE [Part::Feature] Cylinder066  label="Cylinder026"
  Placement = pos=(-1452.15,1029.5,898.834) rot=(0.077196,-0.673675,0.734984;2.61448rad)
  shape: bbox 253.8 x 1010 x 159.4 mm, 3 faces (baked)
FEATURE [Part::Feature] Cylinder067  label="Varilla-B-modif-030"
  Placement = pos=(-1898.23,606.07,20.4541) rot=(0.251906,-0.2009,0.946669;2.02469rad)
  shape: bbox 203 x 603 x 1017 mm, 3 faces (baked)
FEATURE [Part::Feature] Cylinder068  label="Varilla-B-modif-031"
  Placement = pos=(-1705.23,-12.1218,1030.9) rot=(-0.54234,0.821957,-0.173938;3.57234rad)
  shape: bbox 203.8 x 602.3 x 1017 mm, 3 faces (baked)
FEATURE [Part::Feature] Clone001132  label="strutcap142"
  Placement = pos=(-1695.97,-21.9626,1048.2) rot=(-0.287012,0.703678,-0.64997;3.33796rad)
  shape: bbox 21.94 x 32.05 x 20.3 mm, 19 faces (baked)
FEATURE [Part::Feature] Clone001133  label="strutcap143"
  Placement = pos=(-1706.01,-10.9624,1032.01) rot=(-0.109939,0.96532,-0.236791;3.37221rad)
  shape: bbox 24.01 x 26.91 x 31.05 mm, 19 faces (baked)
FEATURE [Part::Feature] Cylinder069  label="Cylinder027"
  Placement = pos=(-1427.84,-1062.95,898.834) rot=(0.452335,-0.492994,0.743203;3.55725rad)
  shape: bbox 887.9 x 551.9 x 159.4 mm, 3 faces (baked)
FEATURE [Part::Feature] Cylinder070  label="Cylinder028"
  Placement = pos=(530.036,-1700.3,896.969) rot=(0.371723,-0.782962,-0.498791;1.70995rad)
  shape: bbox 1035 x 90.15 x 161.3 mm, 3 faces (baked)
FEATURE [Part::Feature] Cylinder071  label="Varilla-B-modif-032"
  Placement = pos=(-515.403,-1625.52,1030.9) rot=(0.903009,-0.3391,0.263791;2.99542rad)
  shape: bbox 513.7 x 377.4 x 1017 mm, 3 faces (baked)
FEATURE [Part::Feature] Cylinder072  label="Varilla-B-modif-033"
  Placement = pos=(-1162.98,-1618.04,20.4541) rot=(0.273237,-0.012278,0.961868;3.22808rad)
  shape: bbox 633.5 x 10.03 x 1017 mm, 3 faces (baked)
FEATURE [Part::Feature] Clone001134  label="strutcap144"
  Placement = pos=(-503.182,-1619.75,1048.2) rot=(0.673934,-0.418028,0.609152;3.75287rad)
  shape: bbox 30.99 x 22.33 x 20.3 mm, 19 faces (baked)
FEATURE [Part::Feature] Clone001135  label="strutcap145"
  Placement = pos=(-516.746,-1625.9,1032.01) rot=(-0.652655,0.712308,-0.258186;3.0512rad)
  shape: bbox 24.88 x 26 x 31.05 mm, 19 faces (baked)
FEATURE [Part::Feature] Cylinder073  label="Cylinder029"
  Placement = pos=(569.712,-1686.43,898.834) rot=(-0.797837,0.161779,-0.580762;1.86862rad)
  shape: bbox 796.1 x 679.1 x 159.4 mm, 3 faces (baked)
FEATURE [Part::Feature] Cylinder074  label="Varilla-B-modif-034"
  Placement = pos=(1179.48,-1606.05,20.4541) rot=(-0.285022,-0.188133,-0.939877;1.85504rad)
  shape: bbox 203 x 603.1 x 1017 mm, 3 faces (baked)
FEATURE [Part::Feature] Clone001136  label="Hub-025"
  Placement = pos=(0.0486416,1986.72,-5e-15) rot=(-0.577341,0.577369,0.577341;2.09437rad)
  shape: bbox 53.16 x 12.4 x 55.6 mm, 28 faces (baked)
FEATURE [Part::Feature] Clone001137  label="strutcap146"
  Placement = pos=(-21.9511,1992.92,0) rot=(0.456975,0.628957,-0.628957;3.99887rad)
  shape: bbox 32.2 x 23.31 x 20 mm, 19 faces (baked)
FEATURE [Part::Feature] Clone001138  label="strutcap147"
  Placement = pos=(-10.9511,1992.92,19.0526) rot=(-0.043067,-0.321506,0.945927;1.61128rad)
  shape: bbox 24.46 x 22.68 x 32.46 mm, 19 faces (baked)
FEATURE [Part::Feature] Clone001139  label="strutcap148"
  Placement = pos=(10.3528,1994.07,19.8831) rot=(0.407648,0.155548,0.899793;1.52684rad)
  shape: bbox 27.6 x 22.68 x 31.62 mm, 19 faces (baked)
FEATURE [Part::Feature] Clone001140  label="strutcap149"
  Placement = pos=(21.7815,1993.01,-2.5e-14) rot=(0.696937,0.507089,0.507089;1.92426rad)
  shape: bbox 32.2 x 23.29 x 20 mm, 19 faces (baked)
FEATURE [Part::Feature] Cylinder075  label="Varilla-B-modif-035"
  Placement = pos=(-1152.6,1625.58,-2.89e-13) rot=(0.456975,0.628957,0.628957;2.28431rad)
  shape: bbox 1134 x 376.9 x 10 mm, 3 faces (baked)
FEATURE [Part::Feature] Clone001141  label="Hub-026"
  Placement = pos=(-1889.47,613.977,-5e-15) rot=(0.702712,-0.111316,-0.702712;3.36331rad)
  shape: bbox 27.47 x 52.09 x 55.6 mm, 28 faces (baked)
FEATURE [Part::Feature] Clone001142  label="strutcap150"
  Placement = pos=(-1898.77,605.432,19.0526) rot=(0.112612,-0.208529,0.971511;2.82156rad)
  shape: bbox 20.37 x 25.38 x 32.46 mm, 19 faces (baked)
FEATURE [Part::Feature] Clone001143  label="strutcap151"
  Placement = pos=(-1902.17,594.971,0) rot=(8e-06,0.707107,-0.707107;3.14161rad)
  shape: bbox 20.3 x 30 x 20 mm, 19 faces (baked)
FEATURE [Part::Feature] Clone001144  label="strutcap152"
  Placement = pos=(-1893.28,626.049,19.8831) rot=(0.168898,0.258947,0.95101;2.70038rad)
  shape: bbox 25.15 x 27.06 x 31.62 mm, 19 faces (baked)
FEATURE [Part::Feature] Clone001145  label="strutcap153"
  Placement = pos=(-1888.73,636.589,-2.5e-14) rot=(0.22342,0.689233,0.689233;2.70197rad)
  shape: bbox 27.81 x 32.24 x 20 mm, 19 faces (baked)
FEATURE [Part::Feature] Clone001146  label="Hub-027"
  Placement = pos=(-1167.76,1607.29,-5e-15) rot=(0.665244,-0.33897,-0.665244;3.79522rad)
  shape: bbox 48.34 x 39.85 x 55.6 mm, 28 faces (baked)
FEATURE [Part::Feature] Clone001147  label="strutcap154"
  Placement = pos=(-1180.31,1605.85,19.0526) rot=(0.047109,-0.257408,0.965154;2.21275rad)
  shape: bbox 22.76 x 25.45 x 32.46 mm, 19 faces (baked)
FEATURE [Part::Feature] Clone001148  label="strutcap155"
  Placement = pos=(-1189.21,1599.38,0) rot=(0.223919,0.689152,-0.689152;3.58216rad)
  shape: bbox 30.09 x 30.59 x 20 mm, 19 faces (baked)
FEATURE [Part::Feature] Clone001149  label="strutcap156"
  Placement = pos=(-1163.75,1619.3,19.8831) rot=(0.270223,0.217936,0.937808;2.10624rad)
  shape: bbox 27.56 x 22.35 x 31.62 mm, 19 faces (baked)
FEATURE [Part::Feature] Clone001150  label="strutcap157"
  Placement = pos=(-1153.87,1625.15,-2.5e-14) rot=(0.456433,0.629154,0.629154;2.28521rad)
  shape: bbox 31.34 x 26 x 20 mm, 19 faces (baked)
FEATURE [Part::Feature] Cylinder076  label="Varilla-B-modif-036"
  Placement = pos=(-1902.18,-593.911,-2.89e-13) rot=(-2e-06,0.707107,0.707107;3.1416rad)
  shape: bbox 10.01 x 1189 x 10 mm, 3 faces (baked)
FEATURE [Part::Feature] Clone001151  label="Hub-028"
  Placement = pos=(-1889.51,-613.843,-5e-15) rot=(-0.702716,-0.111274,0.702716;3.36323rad)
  shape: bbox 27.47 x 52.09 x 55.6 mm, 28 faces (baked)
FEATURE [Part::Feature] Clone001152  label="strutcap158"
  Placement = pos=(-1888.61,-636.682,0) rot=(-0.223903,0.689154,-0.689154;2.70105rad)
  shape: bbox 27.82 x 32.23 x 20 mm, 19 faces (baked)
FEATURE [Part::Feature] Clone001153  label="strutcap159"
  Placement = pos=(-1892.01,-626.22,19.0526) rot=(0.171151,-0.163157,0.971641;3.43228rad)
  shape: bbox 24.41 x 24.08 x 32.46 mm, 19 faces (baked)
FEATURE [Part::Feature] Clone001154  label="strutcap160"
  Placement = pos=(-1899.69,-606.315,19.8831) rot=(0.078906,0.292136,0.953116;3.29902rad)
  shape: bbox 20 x 27.5 x 31.62 mm, 19 faces (baked)
FEATURE [Part::Feature] Clone001155  label="strutcap161"
  Placement = pos=(-1902.21,-595.116,-2.5e-14) rot=(-0.00048,0.707107,0.707107;3.14255rad)
  shape: bbox 20.33 x 30.01 x 20 mm, 19 faces (baked)
FEATURE [Part::Feature] Clone001156  label="Hub-029"
  Placement = pos=(-1167.81,-1607.26,-5e-15) rot=(-0.665251,-0.338942,0.665251;3.79517rad)
  shape: bbox 48.34 x 39.86 x 55.6 mm, 28 faces (baked)
FEATURE [Part::Feature] Clone001157  label="strutcap162"
  Placement = pos=(-1180.46,-1607.15,19.8831) rot=(-0.016336,0.32408,0.945889;3.89619rad)
  shape: bbox 25.27 x 26.79 x 31.62 mm, 19 faces (baked)
FEATURE [Part::Feature] Clone001158  label="strutcap163"
  Placement = pos=(-1189.08,-1599.57,-2.5e-14) rot=(-0.224418,0.689071,0.689071;3.58311rad)
  shape: bbox 30.1 x 30.58 x 20 mm, 19 faces (baked)
FEATURE [Part::Feature] Clone001159  label="strutcap164"
  Placement = pos=(-1162.55,-1618.75,19.0526) rot=(0.234252,-0.112384,0.965658;4.04131rad)
  shape: bbox 25.78 x 20.67 x 32.46 mm, 19 faces (baked)
FEATURE [Part::Feature] Clone001160  label="strutcap165"
  Placement = pos=(-1153.65,-1625.21,0) rot=(-0.456958,0.628963,-0.628963;2.28434rad)
  shape: bbox 31.34 x 25.98 x 20 mm, 19 faces (baked)
FEATURE [Part::Feature] Cylinder077  label="Varilla-B-modif-037"
  Placement = pos=(-22.8736,-1992.61,-2.89e-13) rot=(-0.456985,0.628953,0.628953;3.99889rad)
  shape: bbox 1134 x 376.8 x 10 mm, 3 faces (baked)
FEATURE [Part::Feature] Clone001161  label="Hub-030"
  Placement = pos=(0.0119054,-1986.72,-5e-15) rot=(-0.577354,-0.577343,0.577354;4.18878rad)
  shape: bbox 53.16 x 12.4 x 55.6 mm, 28 faces (baked)
FEATURE [Part::Feature] Clone001162  label="strutcap166"
  Placement = pos=(-10.292,-1994.07,19.8831) rot=(0.137371,-0.359993,-0.922786;1.79868rad)
  shape: bbox 27.6 x 22.68 x 31.62 mm, 19 faces (baked)
FEATURE [Part::Feature] Clone001163  label="strutcap167"
  Placement = pos=(11.0118,-1992.92,19.0526) rot=(-0.317192,0.042484,-0.947409;1.63983rad)
  shape: bbox 24.46 x 22.68 x 32.46 mm, 19 faces (baked)
FEATURE [Part::Feature] Clone001164  label="strutcap168"
  Placement = pos=(22.0118,-1992.92,0) rot=(-0.69746,0.50673,-0.50673;1.92355rad)
  shape: bbox 32.2 x 23.31 x 20 mm, 19 faces (baked)
FEATURE [Part::Feature] Clone001165  label="strutcap169"
  Placement = pos=(-21.7208,-1993.01,-2.5e-14) rot=(-0.457503,0.628765,0.628765;3.99974rad)
  shape: bbox 32.2 x 23.29 x 20 mm, 19 faces (baked)
FEATURE [Part::Feature] Clone001166  label="Hub-031"
  Placement = pos=(1167.8,-1607.27,-5e-15) rot=(0.413386,0.81131,-0.413386;1.77839rad)
  shape: bbox 48.34 x 39.86 x 55.6 mm, 28 faces (baked)
FEATURE [Part::Feature] Clone001167  label="strutcap170"
  Placement = pos=(1163.78,-1619.27,19.8831) rot=(0.326774,-0.405165,-0.85385;1.23636rad)
  shape: bbox 27.56 x 22.35 x 31.62 mm, 19 faces (baked)
FEATURE [Part::Feature] Clone001168  label="strutcap171"
  Placement = pos=(1180.34,-1605.82,19.0526) rot=(-0.455439,-0.083356,-0.886356;1.05951rad)
  shape: bbox 22.76 x 25.45 x 32.46 mm, 19 faces (baked)
FEATURE [Part::Feature] Clone001169  label="strutcap172"
  Placement = pos=(1153.91,-1625.13,-2.5e-14) rot=(0.697993,-0.506363,-0.506363;1.92284rad)
  shape: bbox 31.34 x 26 x 20 mm, 19 faces (baked)
FEATURE [Part::Feature] Clone001170  label="strutcap173"
  Placement = pos=(1189.24,-1599.35,0) rot=(-0.908667,0.295233,-0.295233;1.66643rad)
  shape: bbox 30.09 x 30.59 x 20 mm, 19 faces (baked)
FEATURE [Part::Feature] Cylinder078  label="Varilla-B-modif-038"
  Placement = pos=(1888.01,-637.504,0) rot=(0.908674,-0.295221,-0.295221;1.66642rad)
  shape: bbox 706.8 x 967.7 x 10 mm, 3 faces (baked)
FEATURE [App::DocumentObjectGroup] Group010  label="Estructura"
  Group = -> [Clone031,Clone030,Clone028,Cylinder014,Group011,Clone001005,Clone001006,Clone001010,Cylinder016,Clone002,Clone007,Clone005,Clone008,Clone009,Clone001012,Clone001013,Cylinder017,Clone001007,Clone001014,Clone001009,Clone001008,Cylinder015,Cylinder018,Cylinder020,Cylinder019,Clone001016,Clone001020,Clone001018,Clone001023,Clone001027,Cylinder021,Cylinder022,Clone001031,Clone001030,Clone001033,+181 more]
FEATURE [Part::Part2DObjectPython] Line066  # Draft 2D object (typed FeaturePython)
  ChamferSize = 0
  Closed = false
  End = (324.929,1000.03,1701.28)
  FilletRadius = 0
  Length = 1236.04
  MakeFace = true
  MapMode = 5
  Points = (2) [(1376.39,999.957,1051.5),(324.929,1000.03,1701.28)]
  Start = (1376.39,999.957,1051.5)
  Subdivisions = 0
FEATURE [Part::Part2DObjectPython] Line067  # Draft 2D object (typed FeaturePython)
  ChamferSize = 0
  Closed = false
  End = (1376.39,999.957,1051.5)
  FilletRadius = 0
  Length = 1236.04
  MakeFace = true
  MapMode = 5
  Points = (2) [(324.929,1000.03,1701.28),(1376.39,999.957,1051.5)]
  Start = (324.929,1000.03,1701.28)
  Subdivisions = 0
FEATURE [Part::Part2DObjectPython] Line068  # Draft 2D object (typed FeaturePython)
  ChamferSize = 0
  Closed = false
  End = (552.796,1701.28,894.456)
  FilletRadius = 0
  Length = 1093.08
  MakeFace = true
  MapMode = 5
  Points = (2) [(1376.39,999.957,1051.5),(552.796,1701.28,894.456)]
  Start = (1376.39,999.957,1051.5)
  Subdivisions = 0
FEATURE [Part::Part2DObjectPython] Line069  # Draft 2D object (typed FeaturePython)
  ChamferSize = 0
  Closed = false
  End = (552.796,1701.28,894.456)
  FilletRadius = 0
  Length = 1093
  MakeFace = true
  MapMode = 5
  Points = (2) [(324.929,1000.03,1701.28),(552.796,1701.28,894.456)]
  Start = (324.929,1000.03,1701.28)
  Subdivisions = 0
FEATURE [Part::Part2DObjectPython] Line070  # Draft 2D object (typed FeaturePython)
  ChamferSize = 0
  Closed = false
  End = (-525.738,1618.01,1051.5)
  FilletRadius = 0
  Length = 1093.08
  MakeFace = true
  MapMode = 5
  Points = (2) [(552.796,1701.28,894.456),(-525.738,1618.01,1051.5)]
  Start = (552.796,1701.28,894.456)
  Subdivisions = 0
FEATURE [Part::Part2DObjectPython] Line071  # Draft 2D object (typed FeaturePython)
  ChamferSize = 0
  Closed = false
  End = (324.929,1000.03,1701.28)
  FilletRadius = 0
  Length = 1236.02
  MakeFace = true
  MapMode = 5
  Points = (2) [(-525.738,1618.01,1051.5),(324.929,1000.03,1701.28)]
  Start = (-525.738,1618.01,1051.5)
  Subdivisions = 0
FEATURE [Part::Part2DObjectPython] Line072  # Draft 2D object (typed FeaturePython)
  ChamferSize = 0
  Closed = false
  End = (3.6e-11,2000,0)
  FilletRadius = 0
  Length = 1236.11
  MakeFace = true
  MapMode = 5
  Points = (2) [(-525.738,1618.01,1051.5),(3.56977e-11,2000,0)]
  Start = (-525.738,1618.01,1051.5)
  Subdivisions = 0
FEATURE [Part::Part2DObjectPython] Line073  # Draft 2D object (typed FeaturePython)
  ChamferSize = 0
  Closed = false
  End = (552.796,1701.28,894.456)
  FilletRadius = 0
  Length = 1093.1
  MakeFace = true
  MapMode = 5
  Points = (2) [(3.56977e-11,2000,0),(552.796,1701.28,894.456)]
  Start = (3.6e-11,2000,0)
  Subdivisions = 0
FEATURE [Part::Part2DObjectPython] Line074  # Draft 2D object (typed FeaturePython)
  ChamferSize = 0
  Closed = false
  End = (-525.738,1618.01,1051.5)
  FilletRadius = 0
  Length = 1093.08
  MakeFace = true
  MapMode = 5
  Points = (2) [(552.796,1701.28,894.456),(-525.738,1618.01,1051.5)]
  Start = (552.796,1701.28,894.456)
  Subdivisions = 0
FEATURE [Part::Part2DObjectPython] Line075  # Draft 2D object (typed FeaturePython)
  ChamferSize = 0
  Closed = false
  End = (1175.6,1618.02,0)
  FilletRadius = 0
  Length = 1236.11
  MakeFace = true
  MapMode = 5
  Points = (2) [(1376.39,999.957,1051.5),(1175.6,1618.02,0)]
  Start = (1376.39,999.957,1051.5)
  Subdivisions = 0
FEATURE [Part::Part2DObjectPython] Line076  # Draft 2D object (typed FeaturePython)
  ChamferSize = 0
  Closed = false
  End = (552.796,1701.28,894.456)
  FilletRadius = 0
  Length = 1093.1
  MakeFace = true
  MapMode = 5
  Points = (2) [(1175.6,1618.02,0),(552.796,1701.28,894.456)]
  Start = (1175.6,1618.02,0)
  Subdivisions = 0
FEATURE [Part::Part2DObjectPython] Line077  # Draft 2D object (typed FeaturePython)
  ChamferSize = 0
  Closed = false
  End = (-3.6e-11,2000,0)
  FilletRadius = 0
  Length = 1236.1
  MakeFace = true
  MapMode = 5
  Points = (2) [(1175.6,1618.02,0),(-3.5925e-11,2000,0)]
  Start = (1175.6,1618.02,0)
  Subdivisions = 0
FEATURE [Part::Part2DObjectPython] Line078  # Draft 2D object (typed FeaturePython)
  ChamferSize = 0
  Closed = false
  End = (1175.6,1618.02,0)
  FilletRadius = 0
  Length = 1236.1
  MakeFace = true
  MapMode = 5
  Points = (2) [(1902.16,617.998,0),(1175.6,1618.02,0)]
  Start = (1902.16,617.998,0)
  Subdivisions = 0
FEATURE [Part::Part2DObjectPython] Line079  # Draft 2D object (typed FeaturePython)
  ChamferSize = 0
  Closed = false
  End = (1788.83,-9.65e-10,894.484)
  FilletRadius = 0
  Length = 1092.97
  MakeFace = true
  MapMode = 5
  Points = (2) [(1051.49,1.3321e-09,1701.28),(1788.83,-9.64734e-10,894.484)]
  Start = (1051.49,1.332e-09,1701.28)
  Subdivisions = 0
FEATURE [Part::Part2DObjectPython] Line080  # Draft 2D object (typed FeaturePython)
  ChamferSize = 0
  Closed = false
  End = (1376.39,-999.957,1051.5)
  FilletRadius = 0
  Length = 1093.01
  MakeFace = true
  MapMode = 5
  Points = (2) [(1788.83,-9.64734e-10,894.484),(1376.39,-999.957,1051.5)]
  Start = (1788.83,-9.65e-10,894.484)
  Subdivisions = 0
FEATURE [Part::Part2DObjectPython] Line081  # Draft 2D object (typed FeaturePython)
  ChamferSize = 0
  Closed = false
  End = (1788.83,-9.65e-10,894.484)
  FilletRadius = 0
  Length = 1093.01
  MakeFace = true
  MapMode = 5
  Points = (2) [(1376.39,-999.957,1051.5),(1788.83,-9.64734e-10,894.484)]
  Start = (1376.39,-999.957,1051.5)
  Subdivisions = 0
FEATURE [Part::Part2DObjectPython] Line082  # Draft 2D object (typed FeaturePython)
  ChamferSize = 0
  Closed = false
  End = (1902.16,-617.998,0)
  FilletRadius = 0
  Length = 1093.1
  MakeFace = true
  MapMode = 5
  Points = (2) [(1788.83,-9.64734e-10,894.484),(1902.16,-617.998,0)]
  Start = (1788.83,-9.65e-10,894.484)
  Subdivisions = 0
FEATURE [Part::Part2DObjectPython] Line083  # Draft 2D object (typed FeaturePython)
  ChamferSize = 0
  Closed = false
  End = (1902.16,617.998,0)
  FilletRadius = 0
  Length = 1093.1
  MakeFace = true
  MapMode = 5
  Points = (2) [(1788.83,-9.64734e-10,894.484),(1902.16,617.998,0)]
  Start = (1788.83,-9.65e-10,894.484)
  Subdivisions = 0
FEATURE [Part::Part2DObjectPython] Line084  # Draft 2D object (typed FeaturePython)
  ChamferSize = 0
  Closed = false
  End = (1376.39,999.957,1051.5)
  FilletRadius = 0
  Length = 1093.01
  MakeFace = true
  MapMode = 5
  Points = (2) [(1788.83,-9.64734e-10,894.484),(1376.39,999.957,1051.5)]
  Start = (1788.83,-9.65e-10,894.484)
  Subdivisions = 0
FEATURE [Part::Part2DObjectPython] Line085  # Draft 2D object (typed FeaturePython)
  ChamferSize = 0
  Closed = false
  End = (-525.738,1618.01,1051.5)
  FilletRadius = 0
  Length = 1236.01
  MakeFace = true
  MapMode = 5
  Points = (2) [(-850.675,618.052,1701.28),(-525.738,1618.01,1051.5)]
  Start = (-850.675,618.052,1701.28)
  Subdivisions = 0
FEATURE [Part::Part2DObjectPython] Line086  # Draft 2D object (typed FeaturePython)
  ChamferSize = 0
  Closed = false
  End = (-1175.6,1618.02,0)
  FilletRadius = 0
  Length = 1236.11
  MakeFace = true
  MapMode = 5
  Points = (2) [(-525.738,1618.01,1051.5),(-1175.6,1618.02,0)]
  Start = (-525.738,1618.01,1051.5)
  Subdivisions = 0
FEATURE [Part::Part2DObjectPython] Line087  # Draft 2D object (typed FeaturePython)
  ChamferSize = 0
  Closed = false
  End = (-1175.6,1618.02,0)
  FilletRadius = 0
  Length = 1236.1
  MakeFace = true
  MapMode = 5
  Points = (2) [(3.56977e-11,2000,0),(-1175.6,1618.02,0)]
  Start = (3.6e-11,2000,0)
  Subdivisions = 0
FEATURE [Part::Part2DObjectPython] Line088  # Draft 2D object (typed FeaturePython)
  ChamferSize = 0
  Closed = false
  End = (-1701.28,-1.022e-09,1051.5)
  FilletRadius = 0
  Length = 1236.02
  MakeFace = true
  MapMode = 5
  Points = (2) [(-850.675,618.052,1701.28),(-1701.28,-1.02242e-09,1051.5)]
  Start = (-850.675,618.052,1701.28)
  Subdivisions = 0
FEATURE [Part::Part2DObjectPython] Line089  # Draft 2D object (typed FeaturePython)
  ChamferSize = 0
  Closed = false
  End = (-1175.6,1618.02,0)
  FilletRadius = 0
  Length = 1236.1
  MakeFace = true
  MapMode = 5
  Points = (2) [(-1902.16,617.998,0),(-1175.6,1618.02,0)]
  Start = (-1902.16,617.998,0)
  Subdivisions = 0
FEATURE [Part::Part2DObjectPython] Line090  # Draft 2D object (typed FeaturePython)
  ChamferSize = 0
  Closed = false
  End = (-1447.21,1051.46,894.426)
  FilletRadius = 0
  Length = 1093.05
  MakeFace = true
  MapMode = 5
  Points = (2) [(-525.738,1618.01,1051.5),(-1447.21,1051.46,894.426)]
  Start = (-525.738,1618.01,1051.5)
  Subdivisions = 0
FEATURE [Part::Part2DObjectPython] Line091  # Draft 2D object (typed FeaturePython)
  ChamferSize = 0
  Closed = false
  End = (-1175.6,1618.02,0)
  FilletRadius = 0
  Length = 1093.05
  MakeFace = true
  MapMode = 5
  Points = (2) [(-1447.21,1051.46,894.426),(-1175.6,1618.02,0)]
  Start = (-1447.21,1051.46,894.426)
  Subdivisions = 0
FEATURE [Part::Part2DObjectPython] Line092  # Draft 2D object (typed FeaturePython)
  ChamferSize = 0
  Closed = false
  End = (-1902.16,617.998,0)
  FilletRadius = 0
  Length = 1093.1
  MakeFace = true
  MapMode = 5
  Points = (2) [(-1447.21,1051.46,894.426),(-1902.16,617.998,0)]
  Start = (-1447.21,1051.46,894.426)
  Subdivisions = 0
FEATURE [Part::Part2DObjectPython] Line093  # Draft 2D object (typed FeaturePython)
  ChamferSize = 0
  Closed = false
  End = (-1701.28,-1.022e-09,1051.5)
  FilletRadius = 0
  Length = 1093.07
  MakeFace = true
  MapMode = 5
  Points = (2) [(-1447.21,1051.46,894.426),(-1701.28,-1.02242e-09,1051.5)]
  Start = (-1447.21,1051.46,894.426)
  Subdivisions = 0
FEATURE [Part::Part2DObjectPython] Line094  # Draft 2D object (typed FeaturePython)
  ChamferSize = 0
  Closed = false
  End = (-850.675,618.052,1701.28)
  FilletRadius = 0
  Length = 1093.03
  MakeFace = true
  MapMode = 5
  Points = (2) [(-1447.21,1051.46,894.426),(-850.675,618.052,1701.28)]
  Start = (-1447.21,1051.46,894.426)
  Subdivisions = 0
FEATURE [Part::Part2DObjectPython] Line095  # Draft 2D object (typed FeaturePython)
  ChamferSize = 0
  Closed = false
  End = (-850.675,618.052,1701.28)
  FilletRadius = 0
  Length = 1236.1
  MakeFace = true
  MapMode = 5
  Points = (2) [(324.929,1000.03,1701.28),(-850.675,618.052,1701.28)]
  Start = (324.929,1000.03,1701.28)
  Subdivisions = 0
FEATURE [Part::Part2DObjectPython] Line096  # Draft 2D object (typed FeaturePython)
  ChamferSize = 0
  Closed = false
  End = (-1902.16,617.998,0)
  FilletRadius = 0
  Length = 1236.09
  MakeFace = true
  MapMode = 5
  Points = (2) [(-1701.28,-1.02242e-09,1051.5),(-1902.16,617.998,0)]
  Start = (-1701.28,-1.022e-09,1051.5)
  Subdivisions = 0
FEATURE [Part::Part2DObjectPython] Line097  # Draft 2D object (typed FeaturePython)
  ChamferSize = 0
  Closed = false
  End = (1175.6,-1618.02,0)
  FilletRadius = 0
  Length = 1236.11
  MakeFace = true
  MapMode = 5
  Points = (2) [(1376.39,-999.957,1051.5),(1175.6,-1618.02,0)]
  Start = (1376.39,-999.957,1051.5)
  Subdivisions = 0
FEATURE [Part::Part2DObjectPython] Line098  # Draft 2D object (typed FeaturePython)
  ChamferSize = 0
  Closed = false
  End = (552.796,-1701.28,894.456)
  FilletRadius = 0
  Length = 1093.1
  MakeFace = true
  MapMode = 5
  Points = (2) [(1175.6,-1618.02,0),(552.796,-1701.28,894.456)]
  Start = (1175.6,-1618.02,0)
  Subdivisions = 0
FEATURE [Part::Part2DObjectPython] Line099  # Draft 2D object (typed FeaturePython)
  ChamferSize = 0
  Closed = false
  End = (1376.39,-999.957,1051.5)
  FilletRadius = 0
  Length = 1093.08
  MakeFace = true
  MapMode = 5
  Points = (2) [(552.796,-1701.28,894.456),(1376.39,-999.957,1051.5)]
  Start = (552.796,-1701.28,894.456)
  Subdivisions = 0
FEATURE [Part::Part2DObjectPython] Line100  # Draft 2D object (typed FeaturePython)
  ChamferSize = 0
  Closed = false
  End = (324.937,-1000.03,1701.28)
  FilletRadius = 0
  Length = 1093
  MakeFace = true
  MapMode = 5
  Points = (2) [(552.796,-1701.28,894.456),(324.937,-1000.03,1701.28)]
  Start = (552.796,-1701.28,894.456)
  Subdivisions = 0
FEATURE [Part::Part2DObjectPython] Line101  # Draft 2D object (typed FeaturePython)
  ChamferSize = 0
  Closed = false
  End = (-525.738,-1618.01,1051.5)
  FilletRadius = 0
  Length = 1236.03
  MakeFace = true
  MapMode = 5
  Points = (2) [(324.937,-1000.03,1701.28),(-525.738,-1618.01,1051.5)]
  Start = (324.937,-1000.03,1701.28)
  Subdivisions = 0
FEATURE [Part::Part2DObjectPython] Line102  # Draft 2D object (typed FeaturePython)
  ChamferSize = 0
  Closed = false
  End = (552.796,-1701.28,894.456)
  FilletRadius = 0
  Length = 1093.08
  MakeFace = true
  MapMode = 5
  Points = (2) [(-525.738,-1618.01,1051.5),(552.796,-1701.28,894.456)]
  Start = (-525.738,-1618.01,1051.5)
  Subdivisions = 0
FEATURE [Part::Part2DObjectPython] Line103  # Draft 2D object (typed FeaturePython)
  ChamferSize = 0
  Closed = false
  End = (-3.6e-11,-2000,0)
  FilletRadius = 0
  Length = 1093.1
  MakeFace = true
  MapMode = 5
  Points = (2) [(552.796,-1701.28,894.456),(-3.5925e-11,-2000,0)]
  Start = (552.796,-1701.28,894.456)
  Subdivisions = 0
FEATURE [Part::Part2DObjectPython] Line104  # Draft 2D object (typed FeaturePython)
  ChamferSize = 0
  Closed = false
  End = (1175.6,-1618.02,0)
  FilletRadius = 0
  Length = 1236.1
  MakeFace = true
  MapMode = 5
  Points = (2) [(-3.5925e-11,-2000,0),(1175.6,-1618.02,0)]
  Start = (-3.6e-11,-2000,0)
  Subdivisions = 0
FEATURE [Part::Part2DObjectPython] Line105  # Draft 2D object (typed FeaturePython)
  ChamferSize = 0
  Closed = false
  End = (-525.738,-1618.01,1051.5)
  FilletRadius = 0
  Length = 1236.11
  MakeFace = true
  MapMode = 5
  Points = (2) [(-3.5925e-11,-2000,0),(-525.738,-1618.01,1051.5)]
  Start = (-3.6e-11,-2000,0)
  Subdivisions = 0
FEATURE [Part::Part2DObjectPython] Line106  # Draft 2D object (typed FeaturePython)
  ChamferSize = 0
  Closed = false
  End = (-850.675,-618.052,1701.28)
  FilletRadius = 0
  Length = 1236.02
  MakeFace = true
  MapMode = 5
  Points = (2) [(-1701.28,-1.02242e-09,1051.5),(-850.675,-618.052,1701.28)]
  Start = (-1701.28,-1.022e-09,1051.5)
  Subdivisions = 0
FEATURE [Part::Part2DObjectPython] Line107  # Draft 2D object (typed FeaturePython)
  ChamferSize = 0
  Closed = false
  End = (-1902.16,-617.998,0)
  FilletRadius = 0
  Length = 1236.09
  MakeFace = true
  MapMode = 5
  Points = (2) [(-1701.28,-1.02242e-09,1051.5),(-1902.16,-617.998,0)]
  Start = (-1701.28,-1.022e-09,1051.5)
  Subdivisions = 0
FEATURE [Part::Part2DObjectPython] Line108  # Draft 2D object (typed FeaturePython)
  ChamferSize = 0
  Closed = false
  End = (-1902.16,617.998,0)
  FilletRadius = 0
  Length = 1236
  MakeFace = true
  MapMode = 5
  Points = (2) [(-1902.16,-617.998,0),(-1902.16,617.998,0)]
  Start = (-1902.16,-617.998,0)
  Subdivisions = 0
FEATURE [Part::Part2DObjectPython] Line109  # Draft 2D object (typed FeaturePython)
  ChamferSize = 0
  Closed = false
  End = (-525.738,-1618.01,1051.5)
  FilletRadius = 0
  Length = 1236.01
  MakeFace = true
  MapMode = 5
  Points = (2) [(-850.675,-618.052,1701.28),(-525.738,-1618.01,1051.5)]
  Start = (-850.675,-618.052,1701.28)
  Subdivisions = 0
FEATURE [Part::Part2DObjectPython] Line110  # Draft 2D object (typed FeaturePython)
  ChamferSize = 0
  Closed = false
  End = (-1175.6,-1618.02,0)
  FilletRadius = 0
  Length = 1236.11
  MakeFace = true
  MapMode = 5
  Points = (2) [(-525.738,-1618.01,1051.5),(-1175.6,-1618.02,0)]
  Start = (-525.738,-1618.01,1051.5)
  Subdivisions = 0
FEATURE [Part::Part2DObjectPython] Line111  # Draft 2D object (typed FeaturePython)
  ChamferSize = 0
  Closed = false
  End = (-1902.16,-617.998,0)
  FilletRadius = 0
  Length = 1236.1
  MakeFace = true
  MapMode = 5
  Points = (2) [(-1175.6,-1618.02,0),(-1902.16,-617.998,0)]
  Start = (-1175.6,-1618.02,0)
  Subdivisions = 0
FEATURE [Part::Part2DObjectPython] Line112  # Draft 2D object (typed FeaturePython)
  ChamferSize = 0
  Closed = false
  End = (-1447.19,-1051.45,894.481)
  FilletRadius = 0
  Length = 1093.15
  MakeFace = true
  MapMode = 5
  Points = (2) [(-1902.16,-617.998,0),(-1447.19,-1051.45,894.481)]
  Start = (-1902.16,-617.998,0)
  Subdivisions = 0
FEATURE [Part::Part2DObjectPython] Line113  # Draft 2D object (typed FeaturePython)
  ChamferSize = 0
  Closed = false
  End = (-1701.28,-1.022e-09,1051.5)
  FilletRadius = 0
  Length = 1093.05
  MakeFace = true
  MapMode = 5
  Points = (2) [(-1447.19,-1051.45,894.481),(-1701.28,-1.02242e-09,1051.5)]
  Start = (-1447.19,-1051.45,894.481)
  Subdivisions = 0
FEATURE [Part::Part2DObjectPython] Line114  # Draft 2D object (typed FeaturePython)
  ChamferSize = 0
  Closed = false
  End = (-850.675,-618.052,1701.28)
  FilletRadius = 0
  Length = 1092.97
  MakeFace = true
  MapMode = 5
  Points = (2) [(-1447.19,-1051.45,894.481),(-850.675,-618.052,1701.28)]
  Start = (-1447.19,-1051.45,894.481)
  Subdivisions = 0
FEATURE [Part::Part2DObjectPython] Line115  # Draft 2D object (typed FeaturePython)
  ChamferSize = 0
  Closed = false
  End = (-525.738,-1618.01,1051.5)
  FilletRadius = 0
  Length = 1093.03
  MakeFace = true
  MapMode = 5
  Points = (2) [(-1447.19,-1051.45,894.481),(-525.738,-1618.01,1051.5)]
  Start = (-1447.19,-1051.45,894.481)
  Subdivisions = 0
FEATURE [Part::Part2DObjectPython] Line116  # Draft 2D object (typed FeaturePython)
  ChamferSize = 0
  Closed = false
  End = (-1175.6,-1618.02,0)
  FilletRadius = 0
  Length = 1093.1
  MakeFace = true
  MapMode = 5
  Points = (2) [(-1447.19,-1051.45,894.481),(-1175.6,-1618.02,0)]
  Start = (-1447.19,-1051.45,894.481)
  Subdivisions = 0
FEATURE [Part::Part2DObjectPython] Line117  # Draft 2D object (typed FeaturePython)
  ChamferSize = 0
  Closed = false
  End = (-3.6e-11,-2000,0)
  FilletRadius = 0
  Length = 1236.1
  MakeFace = true
  MapMode = 5
  Points = (2) [(-1175.6,-1618.02,0),(-3.5925e-11,-2000,0)]
  Start = (-1175.6,-1618.02,0)
  Subdivisions = 0
FEATURE [Part::Part2DObjectPython] Line118  # Draft 2D object (typed FeaturePython)
  ChamferSize = 0
  Closed = false
  End = (-850.675,618.052,1701.28)
  FilletRadius = 0
  Length = 1093.1
  MakeFace = true
  MapMode = 5
  Points = (2) [(-1.99876e-10,3.00061e-10,2000),(-850.675,618.052,1701.28)]
  Start = (-2e-10,3e-10,2000)
  Subdivisions = 0
FEATURE [Part::Part2DObjectPython] Line119  # Draft 2D object (typed FeaturePython)
  ChamferSize = 0
  Closed = false
  End = (-850.675,-618.052,1701.28)
  FilletRadius = 0
  Length = 1093.1
  MakeFace = true
  MapMode = 5
  Points = (2) [(-1.99876e-10,3.00061e-10,2000),(-850.675,-618.052,1701.28)]
  Start = (-2e-10,3e-10,2000)
  Subdivisions = 0
FEATURE [Part::Part2DObjectPython] Line120  # Draft 2D object (typed FeaturePython)
  ChamferSize = 0
  Closed = false
  End = (324.937,-1000.03,1701.28)
  FilletRadius = 0
  Length = 1093.1
  MakeFace = true
  MapMode = 5
  Points = (2) [(-1.99876e-10,3.00061e-10,2000),(324.937,-1000.03,1701.28)]
  Start = (-2e-10,3e-10,2000)
  Subdivisions = 0
FEATURE [Part::Part2DObjectPython] Line121  # Draft 2D object (typed FeaturePython)
  ChamferSize = 0
  Closed = false
  End = (1051.49,1.332e-09,1701.28)
  FilletRadius = 0
  Length = 1093.1
  MakeFace = true
  MapMode = 5
  Points = (2) [(-1.99876e-10,3.00061e-10,2000),(1051.49,1.3321e-09,1701.28)]
  Start = (-2e-10,3e-10,2000)
  Subdivisions = 0
FEATURE [Part::Part2DObjectPython] Line122  # Draft 2D object (typed FeaturePython)
  ChamferSize = 0
  Closed = false
  End = (324.929,1000.03,1701.28)
  FilletRadius = 0
  Length = 1093.1
  MakeFace = true
  MapMode = 5
  Points = (2) [(-1.99876e-10,3.00061e-10,2000),(324.929,1000.03,1701.28)]
  Start = (-2e-10,3e-10,2000)
  Subdivisions = 0
FEATURE [App::DocumentObjectGroup] Group013  label="Domo-alambrico"
  Group = -> [Line054,Line055,Line056,Line057,Line058,Line059,Line060,Line061,Line062,Line063,Line064,Line065,Line066,Line067,Line068,Line069,Line070,Line071,Line072,Line073,Line074,Line075,Line076,Line077,Line078,Line079,Line080,Line081,Line082,Line083,Line084,Line085,Line086,Line087,Line088,Line089,Line090,Line091,Line092,Line093,Line094,Line095,Line096,Line097,Line098,Line099,Line100,Line101,Line102,Line103,+19 more]
FEATURE [App::Annotation] Text  label="Texto-Material"
  LabelText = Material
  Position = (3227.54,1318.45,0)
FEATURE [App::FeaturePython] Dimension002  # Draft dimension (typed FeaturePython)
  Dimline = (-3.6e-11,-2000,0)
  Direction = (0,0,0)
  Distance = 4000
  End = (-3.6e-11,-2000,0)
  Normal = (0,0,1)
  Start = (-3.6e-11,2000,0)
FEATURE [App::FeaturePython] Dimension003  # Draft dimension (typed FeaturePython)
  Dimline = (-2e-10,3e-10,0)
  Direction = (0,0,0)
  Distance = 2000
  End = (-2e-10,3e-10,0)
  Normal = (0,-1,0)
  Start = (-2e-10,3e-10,2000)
FEATURE [App::FeaturePython] Dimension004  # Draft dimension (typed FeaturePython)
  Dimline = (2000,-600,0)
  Direction = (0,0,0)
  Distance = 1236
  End = (1902.16,-617.998,0)
  Normal = (0,0,1)
  Start = (1902.16,617.998,0)
FEATURE [App::FeaturePython] Dimension005  # Draft dimension (typed FeaturePython)
  Dimline = (1692.93,0,1177.36)
  Direction = (0,0,0)
  Distance = 1092.97
  End = (1788.83,-9.65e-10,894.484)
  Normal = (0,-1,0)
  Start = (1051.49,1.332e-09,1701.28)
FEATURE [App::DocumentObjectGroup] Group014  label="Dimensions"
  Group = -> [Dimension002,Dimension003,Dimension004,Dimension005]
FEATURE [Part::Feature] Cylinder079  label="Varilla-B-modif-039"
  Placement = pos=(3067.05,988.83,0) rot=(1,1.4e-05,1.4e-05;1.5708rad)
  shape: bbox 10.03 x 1189 x 10 mm, 3 faces (baked)
FEATURE [Part::Feature] Cylinder081  label="Cylinder078"
  Placement = pos=(2871.13,-200,5.93e-10) rot=(-1,0,0;1.5708rad)
  shape: bbox 10 x 1047 x 10 mm, 3 faces (baked)
FEATURE [App::Annotation] Text002  label="Texto-varillas"
  LabelText = Varillas
  Position = (2851.65,1075.67,0)
FEATURE [App::Annotation] Text006  label="Texto-varilla-B"
  LabelText = B
  Position = (3045.54,-293.166,0)
FEATURE [App::Annotation] Text007  label="Texto-varilla-A"
  LabelText = A
  Position = (2839.02,-294.635,0)
FEATURE [Part::Feature] Clone001171  label="Hub5-01-clave008"
  Placement = pos=(3486.66,751.241,9.4e-14) rot=(0,0,-1;0.314151rad)
  shape: bbox 54.38 x 55.6 x 12.4 mm, 25 faces (baked)
FEATURE [Part::Feature] Clone001172  label="Hub-032"
  Placement = pos=(3822.07,752.602,-9.09e-13) rot=(0,0,1;0.523599rad)
  shape: bbox 53.16 x 55.6 x 12.4 mm, 28 faces (baked)
FEATURE [App::Annotation] Text008  label="Texto-Piezas-impresas"
  LabelText = Piezas impresas 3D
  Position = (3335.62,1068.59,0)
FEATURE [App::Annotation] Text009  label="Texto-conector-pentagonal"
  LabelText = Conector | pentagonal
  Position = (3357.25,917.695,0)
FEATURE [App::Annotation] Text010  label="Texto-conector-hexagonal"
  LabelText = Conector | Hexagonal
  Position = (3702.82,917.695,0)
FEATURE [Part::Feature] Clone001176  label="strutcap177"
  Placement = pos=(3662.75,464.083,20) rot=(1,0,0;3.14159rad)
  shape: bbox 20.3 x 20 x 30 mm, 19 faces (baked)
FEATURE [App::Annotation] Text012  label="Texto-varillas005"
  LabelText = Teton
  Position = (3595.02,530.248,0)
FEATURE [Part::Feature] Chamfer002  label="Tuerca-M3"
  Placement = pos=(3453.75,-347.288,0) rot=(1,0,0;1.5708rad)
  shape: bbox 6.35 x 6.35 x 2.4 mm, 29 faces (baked)
FEATURE [Part::Feature] Part__Feature002  label="Tornillo-M3"
  Placement = pos=(3442.59,-46.9489,3) rot=(0,-1,0;1.5708rad)
  shape: bbox 13 x 5.5 x 5.5 mm, 16 faces (baked)
FEATURE [App::Annotation] Text017  label="Texto-x30"
  LabelText = x30
  Position = (2840.67,-387.052,0)
FEATURE [App::Annotation] Text019  label="Texto-x35"
  LabelText = x35
  Position = (3032.11,-387.052,0)
FEATURE [App::Annotation] Text020
  LabelText = Tuercas M3
  Position = (3378.67,-274.428,0)
FEATURE [App::Annotation] Text021
  LabelText = Tornillos M3 x 10mm
  Position = (3372,13.5051,0)
FEATURE [App::Annotation] Text022  label="Texto-x6"
  LabelText = x6
  Position = (3441.07,635.345,0)
FEATURE [App::Annotation] Text023  label="Texto-x20"
  LabelText = x20
  Position = (3785.21,635.345,0)
FEATURE [App::Annotation] Text024  label="Texto-x037"
  LabelText = x160
  Position = (3595.42,372.947,0)
FEATURE [Part::Part2DObjectPython] Rectangle  # Draft 2D object (typed FeaturePython)
  ChamferSize = 0
  Columns = 1
  FilletRadius = 0
  Height = -869.038
  Length = 778.826
  MakeFace = false
  MapMode = 5
  Placement = pos=(3282.79,1174.01,0) rot=(0,0,1;0rad)
  Rows = 1
FEATURE [App::Annotation] Text026  label="Texto-Piezas-impresas002"
  LabelText = Tornilleria
  Position = (3493.63,154.878,0)
FEATURE [Part::Part2DObjectPython] Rectangle003  # Draft 2D object (typed FeaturePython)
  ChamferSize = 0
  Columns = 1
  FilletRadius = 0
  Height = -237.557
  Length = 1305.06
  MakeFace = false
  MapMode = 5
  Placement = pos=(2748.42,1457.07,0) rot=(0,0,1;0rad)
  Rows = 1
FEATURE [App::DocumentObjectGroup] Group017  label="Piezas-impresas"
  Group = -> [Clone001171,Clone001172,Clone001176,Text008,Text022,Text023,Text024,Rectangle,Text009,Text010,Text012]
FEATURE [App::Annotation] Text027  label="Texto-x130"
  LabelText = x130
  Position = (3503.66,-74.9347,0)
FEATURE [App::Annotation] Text028  label="Texto-x131"
  LabelText = x130
  Position = (3509.07,-372.19,0)
FEATURE [Part::Part2DObjectPython] Rectangle004  # Draft 2D object (typed FeaturePython)
  ChamferSize = 0
  Columns = 1
  FilletRadius = 0
  Height = -688.616
  Length = 787.849
  MakeFace = false
  MapMode = 5
  Placement = pos=(3285.28,239.952,0) rot=(0,0,1;0rad)
  Rows = 1
FEATURE [App::DocumentObjectGroup] Group018  label="Tornilleria"
  Group = -> [Text026,Text020,Text021,Part__Feature002,Chamfer002,Text027,Text028,Rectangle004]
FEATURE [Part::Part2DObjectPython] Rectangle005  # Draft 2D object (typed FeaturePython)
  ChamferSize = 0
  Columns = 1
  FilletRadius = 0
  Height = -1623.39
  Length = 466.45
  MakeFace = false
  MapMode = 5
  Placement = pos=(2751.78,1169.58,0) rot=(0,0,1;0rad)
  Rows = 1
FEATURE [App::DocumentObjectGroup] Group016  label="Varillas"
  Group = -> [Cylinder079,Cylinder081,Text002,Text006,Text007,Text017,Text019,Rectangle005]
FEATURE [App::DocumentObjectGroup] Group015  label="Materiales"
  Group = -> [Group016,Text,Group017,Group018,Rectangle003]
FEATURE [Part::Feature] Clone001177  label="strutcap178"
  Placement = pos=(-20,-1.7017e-11,-9.6998e-11) rot=(0.707107,0,0.707107;3.14159rad)
  shape: bbox 30 x 20 x 20.3 mm, 19 faces (baked)
FEATURE [Part::Feature] Part__Feature  label="Tornillo-M004"
  Placement = pos=(-5.55,-1.70132e-11,29.9) rot=(0,0,1;0rad)
  shape: bbox 5.5 x 5.5 x 13 mm, 16 faces (baked)
FEATURE [Part::Feature] Chamfer  label="Tuerca-M004"
  Placement = pos=(9.45,-1.7019e-11,6.96667) rot=(1,0,0;1.5708rad)
  shape: bbox 6.35 x 6.35 x 2.4 mm, 29 faces (baked)
FEATURE [Part::Feature] Cylinder082  label="Varilla-B-modif-040"
  Placement = pos=(16.0356,-0.0024909,5.5791e-06) rot=(0.57734,0.577355,0.577355;2.09441rad)
  shape: bbox 1189 x 10.03 x 10 mm, 3 faces (baked)
FEATURE [Part::Part2DObjectPython] Line124  # Draft 2D object (typed FeaturePython)
  ChamferSize = 0
  Closed = false
  End = (-5.55,-1.7e-11,6.56667)
  FilletRadius = 0
  Length = 2.8
  MakeFace = true
  MapMode = 5
  Points = (2) [(-5.55,-1.70175e-11,9.36667),(-5.55,-1.70176e-11,6.56667)]
  Start = (-5.55,-1.7e-11,9.36667)
  Subdivisions = 0
  Support = -> [Clone001177]
FEATURE [Part::Part2DObjectPython] Line125  # Draft 2D object (typed FeaturePython)
  ChamferSize = 0
  Closed = false
  End = (6.7,-1.7e-11,8.16667)
  FilletRadius = 0
  Length = 12.2516
  MakeFace = true
  MapMode = 5
  Points = (2) [(-5.55,-1.70176e-11,7.96667),(6.7,-1.70192e-11,8.16667)]
  Start = (-5.55,-1.7e-11,7.96667)
  Subdivisions = 0
FEATURE [Part::Part2DObjectPython] Line126  # Draft 2D object (typed FeaturePython)
  ChamferSize = 0
  Closed = false
  End = (-5.55,-1.7e-11,7.96667)
  FilletRadius = 0
  Length = 11.9333
  MakeFace = true
  MapMode = 5
  Points = (2) [(-5.55,-1.70177e-11,19.9),(-5.55,-1.70176e-11,7.96667)]
  Start = (-5.55,-1.7e-11,19.9)
  Subdivisions = 0
FEATURE [Part::Part2DObjectPython] Line127  # Draft 2D object (typed FeaturePython)
  ChamferSize = 0
  Closed = false
  End = (-5.55,-1.7e-11,6.56667)
  FilletRadius = 0
  Length = 1.6
  MakeFace = true
  MapMode = 5
  Points = (2) [(-5.55,-1.6,6.56667),(-5.55,-1.70176e-11,6.56667)]
  Start = (-5.55,-1.6,6.56667)
  Subdivisions = 0
FEATURE [App::DocumentObjectGroup] Group020  label="Despiece"
  Group = -> [Clone001177,Part__Feature,Chamfer,Cylinder082,Line124,Line125,Line126,Line127]
FEATURE [Part::Feature] Clone001178  label="strutcap179"
  Placement = pos=(-20,31.6617,-9.6998e-11) rot=(0.707107,0,0.707107;3.14159rad)
  shape: bbox 30 x 20 x 20.3 mm, 19 faces (baked)
FEATURE [Part::Feature] Part__Feature003  label="Tornillo-M005"
  Placement = pos=(-5.55,31.6617,11.9) rot=(0,0,1;0rad)
  shape: bbox 5.5 x 5.5 x 13 mm, 16 faces (baked)
FEATURE [Part::Feature] Chamfer003  label="Tuerca-M005"
  Placement = pos=(-5.55,31.6617,6.96667) rot=(1,0,0;1.5708rad)
  shape: bbox 6.35 x 6.35 x 2.4 mm, 29 faces (baked)
FEATURE [Part::Feature] Cylinder083  label="Varilla-B-modif-041"
  Placement = pos=(-20,31.6617,5.5791e-06) rot=(0.57734,0.577355,0.577355;2.09441rad)
  shape: bbox 1189 x 10.03 x 10 mm, 3 faces (baked)
FEATURE [App::DocumentObjectGroup] Group021  label="Ensamblaje"
  Group = -> [Clone001178,Part__Feature003,Chamfer003,Cylinder083]
FEATURE [App::DocumentObjectGroup] Group019  label="Ensamblaje-tetones"
  Group = -> [Group020,Group021]
